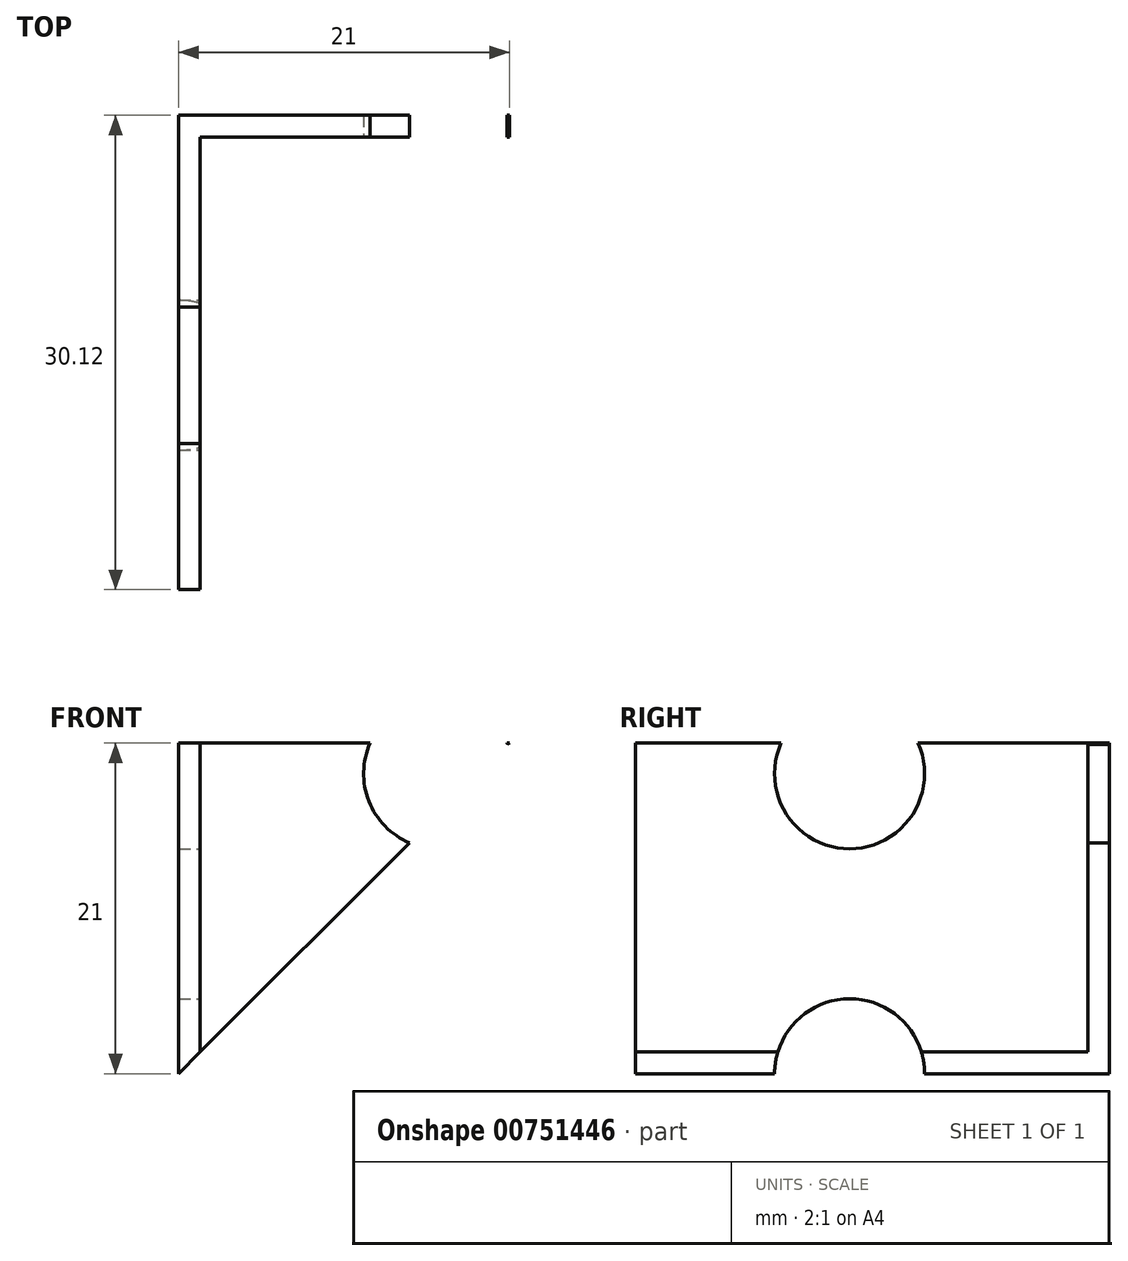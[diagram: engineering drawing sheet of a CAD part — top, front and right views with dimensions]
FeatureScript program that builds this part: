
annotation { "Feature Type Name" : "Feature", "Feature Type Description" : "" }
export const myFeature = defineFeature(function(context is Context, id is Id, definition is map)
    precondition{}
    {
        {
            assignVariable(context, id + "F0", {"name" : "height", "anyValue" : 21});
        }
        {
            var Q0;
            Q0=qCreatedBy(makeId("Top.planeOp"),FACE);
            var sketch = newSketch(context, id + "F1", { "sketchPlane" : qUnion([Q0])});
            skLineSegment(sketch, "E0", {"start": v(-1.37, -28.75) * mm, "end": v(-1.37, 1.37) * mm});
            skLineSegment(sketch, "E1", {"start": v(-1.37, 1.37) * mm, "end": v(28.75, 1.37) * mm});
            skLineSegment(sketch, "E2", {"start": v(28.75, 1.37) * mm, "end": v(28.75, 0) * mm});
            skLineSegment(sketch, "E3", {"start": v(28.75, 0) * mm, "end": v(0, 0) * mm});
            skLineSegment(sketch, "E4", {"start": v(0, 0) * mm, "end": v(0, -28.75) * mm});
            skLineSegment(sketch, "E5", {"start": v(0, -28.75) * mm, "end": v(-1.37, -28.75) * mm});
            skSolve(sketch);
        }
        {
            var Q0;
            Q0=makeQuery(id+"F1.imprint","IMPRINT",FACE,{"disambiguationData":[TD([[makeQuery(id+"F1.imprint","IMPRINT",EDGE,{"derivedFrom":sQuery(id+"F1.wireOp",EDGE,"E0")}),-1.0]])]});
            extrude(context, id + "F2", {"entities" : qUnion([Q0]), "depth" : (getVariable(context, 'height')) * mm, "offsetDistance" : 25.4 * mm});
        }
        {
            var Q0;
            Q0=makeQuery(id+"F2.opExtrude","SWEPT_FACE",FACE,{"disambiguationData":[OSD([sQuery(id+"F1.wireOp",EDGE,"E3")])]});
            var sketch = newSketch(context, id + "F3", { "sketchPlane" : qUnion([Q0])});
            skPoint(sketch, "E6", {"position": v(15.14, 19.05) * mm});
            skLineSegment(sketch, "E7", {"start": v(15.14, 0) * mm, "end": v(15.14, 533.4) * mm, "construction": true});
            skCircle(sketch, "E8", {"center": v(15.14, 19.05) * mm, "radius": 4.76 * mm});
            skCircle(sketch, "E9", {"center": v(15.14, 0) * mm, "radius": 4.76 * mm});
            skPoint(sketch, "E10", {"position": v(15.14, 38.1) * mm});
            skPoint(sketch, "E11", {"position": v(15.14, 57.15) * mm});
            skArc(sketch, "E12", {"start": v(19.9, 39.69) * mm, "mid": v(15.14, 44.45) * mm, "end": v(10.38, 39.69) * mm});
            skArc(sketch, "E13", {"start": v(10.38, 36.51) * mm, "mid": v(15.14, 31.75) * mm, "end": v(19.9, 36.51) * mm});
            skLineSegment(sketch, "E14", {"start": v(19.9, 39.69) * mm, "end": v(19.9, 36.51) * mm});
            skLineSegment(sketch, "E15", {"start": v(10.38, 39.69) * mm, "end": v(10.38, 36.51) * mm});
            skArc(sketch, "E16", {"start": v(19.9, 58.74) * mm, "mid": v(15.14, 63.5) * mm, "end": v(10.38, 58.74) * mm});
            skArc(sketch, "E17", {"start": v(10.38, 55.56) * mm, "mid": v(15.14, 50.8) * mm, "end": v(19.9, 55.56) * mm});
            skLineSegment(sketch, "E18", {"start": v(19.9, 58.74) * mm, "end": v(19.9, 55.56) * mm});
            skLineSegment(sketch, "E19", {"start": v(10.38, 58.74) * mm, "end": v(10.38, 55.56) * mm});
            skPoint(sketch, "E20.0.1.0", {"position": v(15.14, 133.35) * mm});
            skArc(sketch, "E20.0.1.1", {"start": v(19.9, 134.94) * mm, "mid": v(15.14, 139.7) * mm, "end": v(10.38, 134.94) * mm});
            skPoint(sketch, "E20.0.1.2", {"position": v(15.14, 114.3) * mm});
            skPoint(sketch, "E20.0.1.3", {"position": v(15.14, 95.25) * mm});
            skArc(sketch, "E20.0.1.4", {"start": v(10.38, 131.76) * mm, "mid": v(15.14, 127) * mm, "end": v(19.9, 131.76) * mm});
            skCircle(sketch, "E20.0.1.5", {"center": v(15.14, 95.25) * mm, "radius": 4.76 * mm});
            skCircle(sketch, "E20.0.1.6", {"center": v(15.14, 76.2) * mm, "radius": 4.76 * mm});
            skArc(sketch, "E20.0.1.7", {"start": v(19.9, 115.89) * mm, "mid": v(15.14, 120.65) * mm, "end": v(10.38, 115.89) * mm});
            skArc(sketch, "E20.0.1.8", {"start": v(10.38, 112.71) * mm, "mid": v(15.14, 107.95) * mm, "end": v(19.9, 112.71) * mm});
            skPoint(sketch, "E20.0.1.9", {"position": v(15.14, 133.35) * mm});
            skPoint(sketch, "E20.0.1.10", {"position": v(15.14, 114.3) * mm});
            skLineSegment(sketch, "E20.0.1.11", {"start": v(10.38, 134.94) * mm, "end": v(10.38, 131.76) * mm});
            skLineSegment(sketch, "E20.0.1.12", {"start": v(19.9, 134.94) * mm, "end": v(19.9, 131.76) * mm});
            skLineSegment(sketch, "E20.0.1.13", {"start": v(19.9, 115.89) * mm, "end": v(19.9, 112.71) * mm});
            skLineSegment(sketch, "E20.0.1.14", {"start": v(10.38, 115.89) * mm, "end": v(10.38, 112.71) * mm});
            skPoint(sketch, "E20.0.2.0", {"position": v(15.14, 209.55) * mm});
            skArc(sketch, "E20.0.2.1", {"start": v(19.9, 211.14) * mm, "mid": v(15.14, 215.9) * mm, "end": v(10.38, 211.14) * mm});
            skPoint(sketch, "E20.0.2.2", {"position": v(15.14, 190.5) * mm});
            skPoint(sketch, "E20.0.2.3", {"position": v(15.14, 171.45) * mm});
            skArc(sketch, "E20.0.2.4", {"start": v(10.38, 207.96) * mm, "mid": v(15.14, 203.2) * mm, "end": v(19.9, 207.96) * mm});
            skCircle(sketch, "E20.0.2.5", {"center": v(15.14, 171.45) * mm, "radius": 4.76 * mm});
            skCircle(sketch, "E20.0.2.6", {"center": v(15.14, 152.4) * mm, "radius": 4.76 * mm});
            skArc(sketch, "E20.0.2.7", {"start": v(19.9, 192.09) * mm, "mid": v(15.14, 196.85) * mm, "end": v(10.38, 192.09) * mm});
            skArc(sketch, "E20.0.2.8", {"start": v(10.38, 188.91) * mm, "mid": v(15.14, 184.15) * mm, "end": v(19.9, 188.91) * mm});
            skPoint(sketch, "E20.0.2.9", {"position": v(15.14, 209.55) * mm});
            skPoint(sketch, "E20.0.2.10", {"position": v(15.14, 190.5) * mm});
            skLineSegment(sketch, "E20.0.2.11", {"start": v(10.38, 211.14) * mm, "end": v(10.38, 207.96) * mm});
            skLineSegment(sketch, "E20.0.2.12", {"start": v(19.9, 211.14) * mm, "end": v(19.9, 207.96) * mm});
            skLineSegment(sketch, "E20.0.2.13", {"start": v(19.9, 192.09) * mm, "end": v(19.9, 188.91) * mm});
            skLineSegment(sketch, "E20.0.2.14", {"start": v(10.38, 192.09) * mm, "end": v(10.38, 188.91) * mm});
            skPoint(sketch, "E20.0.3.0", {"position": v(15.14, 285.75) * mm});
            skArc(sketch, "E20.0.3.1", {"start": v(19.9, 287.34) * mm, "mid": v(15.14, 292.1) * mm, "end": v(10.38, 287.34) * mm});
            skPoint(sketch, "E20.0.3.2", {"position": v(15.14, 266.7) * mm});
            skPoint(sketch, "E20.0.3.3", {"position": v(15.14, 247.65) * mm});
            skArc(sketch, "E20.0.3.4", {"start": v(10.38, 284.16) * mm, "mid": v(15.14, 279.4) * mm, "end": v(19.9, 284.16) * mm});
            skCircle(sketch, "E20.0.3.5", {"center": v(15.14, 247.65) * mm, "radius": 4.76 * mm});
            skCircle(sketch, "E20.0.3.6", {"center": v(15.14, 228.6) * mm, "radius": 4.76 * mm});
            skArc(sketch, "E20.0.3.7", {"start": v(19.9, 268.29) * mm, "mid": v(15.14, 273.05) * mm, "end": v(10.38, 268.29) * mm});
            skArc(sketch, "E20.0.3.8", {"start": v(10.38, 265.11) * mm, "mid": v(15.14, 260.35) * mm, "end": v(19.9, 265.11) * mm});
            skPoint(sketch, "E20.0.3.9", {"position": v(15.14, 285.75) * mm});
            skPoint(sketch, "E20.0.3.10", {"position": v(15.14, 266.7) * mm});
            skLineSegment(sketch, "E20.0.3.11", {"start": v(10.38, 287.34) * mm, "end": v(10.38, 284.16) * mm});
            skLineSegment(sketch, "E20.0.3.12", {"start": v(19.9, 287.34) * mm, "end": v(19.9, 284.16) * mm});
            skLineSegment(sketch, "E20.0.3.13", {"start": v(19.9, 268.29) * mm, "end": v(19.9, 265.11) * mm});
            skLineSegment(sketch, "E20.0.3.14", {"start": v(10.38, 268.29) * mm, "end": v(10.38, 265.11) * mm});
            skPoint(sketch, "E20.0.4.0", {"position": v(15.14, 361.95) * mm});
            skArc(sketch, "E20.0.4.1", {"start": v(19.9, 363.54) * mm, "mid": v(15.14, 368.3) * mm, "end": v(10.38, 363.54) * mm});
            skPoint(sketch, "E20.0.4.2", {"position": v(15.14, 342.9) * mm});
            skPoint(sketch, "E20.0.4.3", {"position": v(15.14, 323.85) * mm});
            skArc(sketch, "E20.0.4.4", {"start": v(10.38, 360.36) * mm, "mid": v(15.14, 355.6) * mm, "end": v(19.9, 360.36) * mm});
            skCircle(sketch, "E20.0.4.5", {"center": v(15.14, 323.85) * mm, "radius": 4.76 * mm});
            skCircle(sketch, "E20.0.4.6", {"center": v(15.14, 304.8) * mm, "radius": 4.76 * mm});
            skArc(sketch, "E20.0.4.7", {"start": v(19.9, 344.49) * mm, "mid": v(15.14, 349.25) * mm, "end": v(10.38, 344.49) * mm});
            skArc(sketch, "E20.0.4.8", {"start": v(10.38, 341.31) * mm, "mid": v(15.14, 336.55) * mm, "end": v(19.9, 341.31) * mm});
            skPoint(sketch, "E20.0.4.9", {"position": v(15.14, 361.95) * mm});
            skPoint(sketch, "E20.0.4.10", {"position": v(15.14, 342.9) * mm});
            skLineSegment(sketch, "E20.0.4.11", {"start": v(10.38, 363.54) * mm, "end": v(10.38, 360.36) * mm});
            skLineSegment(sketch, "E20.0.4.12", {"start": v(19.9, 363.54) * mm, "end": v(19.9, 360.36) * mm});
            skLineSegment(sketch, "E20.0.4.13", {"start": v(19.9, 344.49) * mm, "end": v(19.9, 341.31) * mm});
            skLineSegment(sketch, "E20.0.4.14", {"start": v(10.38, 344.49) * mm, "end": v(10.38, 341.31) * mm});
            skPoint(sketch, "E20.0.5.0", {"position": v(15.14, 438.15) * mm});
            skArc(sketch, "E20.0.5.1", {"start": v(19.9, 439.74) * mm, "mid": v(15.14, 444.5) * mm, "end": v(10.38, 439.74) * mm});
            skPoint(sketch, "E20.0.5.2", {"position": v(15.14, 419.1) * mm});
            skPoint(sketch, "E20.0.5.3", {"position": v(15.14, 400.05) * mm});
            skArc(sketch, "E20.0.5.4", {"start": v(10.38, 436.56) * mm, "mid": v(15.14, 431.8) * mm, "end": v(19.9, 436.56) * mm});
            skCircle(sketch, "E20.0.5.5", {"center": v(15.14, 400.05) * mm, "radius": 4.76 * mm});
            skCircle(sketch, "E20.0.5.6", {"center": v(15.14, 381) * mm, "radius": 4.76 * mm});
            skArc(sketch, "E20.0.5.7", {"start": v(19.9, 420.69) * mm, "mid": v(15.14, 425.45) * mm, "end": v(10.38, 420.69) * mm});
            skArc(sketch, "E20.0.5.8", {"start": v(10.38, 417.51) * mm, "mid": v(15.14, 412.75) * mm, "end": v(19.9, 417.51) * mm});
            skPoint(sketch, "E20.0.5.9", {"position": v(15.14, 438.15) * mm});
            skPoint(sketch, "E20.0.5.10", {"position": v(15.14, 419.1) * mm});
            skLineSegment(sketch, "E20.0.5.11", {"start": v(10.38, 439.74) * mm, "end": v(10.38, 436.56) * mm});
            skLineSegment(sketch, "E20.0.5.12", {"start": v(19.9, 439.74) * mm, "end": v(19.9, 436.56) * mm});
            skLineSegment(sketch, "E20.0.5.13", {"start": v(19.9, 420.69) * mm, "end": v(19.9, 417.51) * mm});
            skLineSegment(sketch, "E20.0.5.14", {"start": v(10.38, 420.69) * mm, "end": v(10.38, 417.51) * mm});
            skPoint(sketch, "E20.0.6.0", {"position": v(15.14, 514.35) * mm});
            skArc(sketch, "E20.0.6.1", {"start": v(19.9, 515.94) * mm, "mid": v(15.14, 520.7) * mm, "end": v(10.38, 515.94) * mm});
            skPoint(sketch, "E20.0.6.2", {"position": v(15.14, 495.3) * mm});
            skPoint(sketch, "E20.0.6.3", {"position": v(15.14, 476.25) * mm});
            skArc(sketch, "E20.0.6.4", {"start": v(10.38, 512.76) * mm, "mid": v(15.14, 508) * mm, "end": v(19.9, 512.76) * mm});
            skCircle(sketch, "E20.0.6.5", {"center": v(15.14, 476.25) * mm, "radius": 4.76 * mm});
            skCircle(sketch, "E20.0.6.6", {"center": v(15.14, 457.2) * mm, "radius": 4.76 * mm});
            skArc(sketch, "E20.0.6.7", {"start": v(19.9, 496.89) * mm, "mid": v(15.14, 501.65) * mm, "end": v(10.38, 496.89) * mm});
            skArc(sketch, "E20.0.6.8", {"start": v(10.38, 493.71) * mm, "mid": v(15.14, 488.95) * mm, "end": v(19.9, 493.71) * mm});
            skPoint(sketch, "E20.0.6.9", {"position": v(15.14, 514.35) * mm});
            skPoint(sketch, "E20.0.6.10", {"position": v(15.14, 495.3) * mm});
            skLineSegment(sketch, "E20.0.6.11", {"start": v(10.38, 515.94) * mm, "end": v(10.38, 512.76) * mm});
            skLineSegment(sketch, "E20.0.6.12", {"start": v(19.9, 515.94) * mm, "end": v(19.9, 512.76) * mm});
            skLineSegment(sketch, "E20.0.6.13", {"start": v(19.9, 496.89) * mm, "end": v(19.9, 493.71) * mm});
            skLineSegment(sketch, "E20.0.6.14", {"start": v(10.38, 496.89) * mm, "end": v(10.38, 493.71) * mm});
            skPoint(sketch, "E20.0.7.0", {"position": v(15.14, 590.55) * mm});
            skArc(sketch, "E20.0.7.1", {"start": v(19.9, 592.14) * mm, "mid": v(15.14, 596.9) * mm, "end": v(10.38, 592.14) * mm});
            skPoint(sketch, "E20.0.7.2", {"position": v(15.14, 571.5) * mm});
            skPoint(sketch, "E20.0.7.3", {"position": v(15.14, 552.45) * mm});
            skArc(sketch, "E20.0.7.4", {"start": v(10.38, 588.96) * mm, "mid": v(15.14, 584.2) * mm, "end": v(19.9, 588.96) * mm});
            skCircle(sketch, "E20.0.7.5", {"center": v(15.14, 552.45) * mm, "radius": 4.76 * mm});
            skCircle(sketch, "E20.0.7.6", {"center": v(15.14, 533.4) * mm, "radius": 4.76 * mm});
            skArc(sketch, "E20.0.7.7", {"start": v(19.9, 573.09) * mm, "mid": v(15.14, 577.85) * mm, "end": v(10.38, 573.09) * mm});
            skArc(sketch, "E20.0.7.8", {"start": v(10.38, 569.91) * mm, "mid": v(15.14, 565.15) * mm, "end": v(19.9, 569.91) * mm});
            skPoint(sketch, "E20.0.7.9", {"position": v(15.14, 590.55) * mm});
            skPoint(sketch, "E20.0.7.10", {"position": v(15.14, 571.5) * mm});
            skLineSegment(sketch, "E20.0.7.11", {"start": v(10.38, 592.14) * mm, "end": v(10.38, 588.96) * mm});
            skLineSegment(sketch, "E20.0.7.12", {"start": v(19.9, 592.14) * mm, "end": v(19.9, 588.96) * mm});
            skLineSegment(sketch, "E20.0.7.13", {"start": v(19.9, 573.09) * mm, "end": v(19.9, 569.91) * mm});
            skLineSegment(sketch, "E20.0.7.14", {"start": v(10.38, 573.09) * mm, "end": v(10.38, 569.91) * mm});
            skPoint(sketch, "E20.0.8.0", {"position": v(15.14, 666.75) * mm});
            skArc(sketch, "E20.0.8.1", {"start": v(19.9, 668.34) * mm, "mid": v(15.14, 673.1) * mm, "end": v(10.38, 668.34) * mm});
            skPoint(sketch, "E20.0.8.2", {"position": v(15.14, 647.7) * mm});
            skPoint(sketch, "E20.0.8.3", {"position": v(15.14, 628.65) * mm});
            skArc(sketch, "E20.0.8.4", {"start": v(10.38, 665.16) * mm, "mid": v(15.14, 660.4) * mm, "end": v(19.9, 665.16) * mm});
            skCircle(sketch, "E20.0.8.5", {"center": v(15.14, 628.65) * mm, "radius": 4.76 * mm});
            skCircle(sketch, "E20.0.8.6", {"center": v(15.14, 609.6) * mm, "radius": 4.76 * mm});
            skArc(sketch, "E20.0.8.7", {"start": v(19.9, 649.29) * mm, "mid": v(15.14, 654.05) * mm, "end": v(10.38, 649.29) * mm});
            skArc(sketch, "E20.0.8.8", {"start": v(10.38, 646.11) * mm, "mid": v(15.14, 641.35) * mm, "end": v(19.9, 646.11) * mm});
            skPoint(sketch, "E20.0.8.9", {"position": v(15.14, 666.75) * mm});
            skPoint(sketch, "E20.0.8.10", {"position": v(15.14, 647.7) * mm});
            skLineSegment(sketch, "E20.0.8.11", {"start": v(10.38, 668.34) * mm, "end": v(10.38, 665.16) * mm});
            skLineSegment(sketch, "E20.0.8.12", {"start": v(19.9, 668.34) * mm, "end": v(19.9, 665.16) * mm});
            skLineSegment(sketch, "E20.0.8.13", {"start": v(19.9, 649.29) * mm, "end": v(19.9, 646.11) * mm});
            skLineSegment(sketch, "E20.0.8.14", {"start": v(10.38, 649.29) * mm, "end": v(10.38, 646.11) * mm});
            skPoint(sketch, "E20.0.9.0", {"position": v(15.14, 742.95) * mm});
            skArc(sketch, "E20.0.9.1", {"start": v(19.9, 744.54) * mm, "mid": v(15.14, 749.3) * mm, "end": v(10.38, 744.54) * mm});
            skPoint(sketch, "E20.0.9.2", {"position": v(15.14, 723.9) * mm});
            skPoint(sketch, "E20.0.9.3", {"position": v(15.14, 704.85) * mm});
            skArc(sketch, "E20.0.9.4", {"start": v(10.38, 741.36) * mm, "mid": v(15.14, 736.6) * mm, "end": v(19.9, 741.36) * mm});
            skCircle(sketch, "E20.0.9.5", {"center": v(15.14, 704.85) * mm, "radius": 4.76 * mm});
            skCircle(sketch, "E20.0.9.6", {"center": v(15.14, 685.8) * mm, "radius": 4.76 * mm});
            skArc(sketch, "E20.0.9.7", {"start": v(19.9, 725.49) * mm, "mid": v(15.14, 730.25) * mm, "end": v(10.38, 725.49) * mm});
            skArc(sketch, "E20.0.9.8", {"start": v(10.38, 722.31) * mm, "mid": v(15.14, 717.55) * mm, "end": v(19.9, 722.31) * mm});
            skPoint(sketch, "E20.0.9.9", {"position": v(15.14, 742.95) * mm});
            skPoint(sketch, "E20.0.9.10", {"position": v(15.14, 723.9) * mm});
            skLineSegment(sketch, "E20.0.9.11", {"start": v(10.38, 744.54) * mm, "end": v(10.38, 741.36) * mm});
            skLineSegment(sketch, "E20.0.9.12", {"start": v(19.9, 744.54) * mm, "end": v(19.9, 741.36) * mm});
            skLineSegment(sketch, "E20.0.9.13", {"start": v(19.9, 725.49) * mm, "end": v(19.9, 722.31) * mm});
            skLineSegment(sketch, "E20.0.9.14", {"start": v(10.38, 725.49) * mm, "end": v(10.38, 722.31) * mm});
            skPoint(sketch, "E20.0.10.0", {"position": v(15.14, 819.15) * mm});
            skArc(sketch, "E20.0.10.1", {"start": v(19.9, 820.74) * mm, "mid": v(15.14, 825.5) * mm, "end": v(10.38, 820.74) * mm});
            skPoint(sketch, "E20.0.10.2", {"position": v(15.14, 800.1) * mm});
            skPoint(sketch, "E20.0.10.3", {"position": v(15.14, 781.05) * mm});
            skArc(sketch, "E20.0.10.4", {"start": v(10.38, 817.56) * mm, "mid": v(15.14, 812.8) * mm, "end": v(19.9, 817.56) * mm});
            skCircle(sketch, "E20.0.10.5", {"center": v(15.14, 781.05) * mm, "radius": 4.76 * mm});
            skCircle(sketch, "E20.0.10.6", {"center": v(15.14, 762) * mm, "radius": 4.76 * mm});
            skArc(sketch, "E20.0.10.7", {"start": v(19.9, 801.69) * mm, "mid": v(15.14, 806.45) * mm, "end": v(10.38, 801.69) * mm});
            skArc(sketch, "E20.0.10.8", {"start": v(10.38, 798.51) * mm, "mid": v(15.14, 793.75) * mm, "end": v(19.9, 798.51) * mm});
            skPoint(sketch, "E20.0.10.9", {"position": v(15.14, 819.15) * mm});
            skPoint(sketch, "E20.0.10.10", {"position": v(15.14, 800.1) * mm});
            skLineSegment(sketch, "E20.0.10.11", {"start": v(10.38, 820.74) * mm, "end": v(10.38, 817.56) * mm});
            skLineSegment(sketch, "E20.0.10.12", {"start": v(19.9, 820.74) * mm, "end": v(19.9, 817.56) * mm});
            skLineSegment(sketch, "E20.0.10.13", {"start": v(19.9, 801.69) * mm, "end": v(19.9, 798.51) * mm});
            skLineSegment(sketch, "E20.0.10.14", {"start": v(10.38, 801.69) * mm, "end": v(10.38, 798.51) * mm});
            skPoint(sketch, "E20.0.11.0", {"position": v(15.14, 895.35) * mm});
            skArc(sketch, "E20.0.11.1", {"start": v(19.9, 896.94) * mm, "mid": v(15.14, 901.7) * mm, "end": v(10.38, 896.94) * mm});
            skPoint(sketch, "E20.0.11.2", {"position": v(15.14, 876.3) * mm});
            skPoint(sketch, "E20.0.11.3", {"position": v(15.14, 857.25) * mm});
            skArc(sketch, "E20.0.11.4", {"start": v(10.38, 893.76) * mm, "mid": v(15.14, 889) * mm, "end": v(19.9, 893.76) * mm});
            skCircle(sketch, "E20.0.11.5", {"center": v(15.14, 857.25) * mm, "radius": 4.76 * mm});
            skCircle(sketch, "E20.0.11.6", {"center": v(15.14, 838.2) * mm, "radius": 4.76 * mm});
            skArc(sketch, "E20.0.11.7", {"start": v(19.9, 877.89) * mm, "mid": v(15.14, 882.65) * mm, "end": v(10.38, 877.89) * mm});
            skArc(sketch, "E20.0.11.8", {"start": v(10.38, 874.71) * mm, "mid": v(15.14, 869.95) * mm, "end": v(19.9, 874.71) * mm});
            skPoint(sketch, "E20.0.11.9", {"position": v(15.14, 895.35) * mm});
            skPoint(sketch, "E20.0.11.10", {"position": v(15.14, 876.3) * mm});
            skLineSegment(sketch, "E20.0.11.11", {"start": v(10.38, 896.94) * mm, "end": v(10.38, 893.76) * mm});
            skLineSegment(sketch, "E20.0.11.12", {"start": v(19.9, 896.94) * mm, "end": v(19.9, 893.76) * mm});
            skLineSegment(sketch, "E20.0.11.13", {"start": v(19.9, 877.89) * mm, "end": v(19.9, 874.71) * mm});
            skLineSegment(sketch, "E20.0.11.14", {"start": v(10.38, 877.89) * mm, "end": v(10.38, 874.71) * mm});
            skPoint(sketch, "E20.0.12.0", {"position": v(15.14, 971.55) * mm});
            skArc(sketch, "E20.0.12.1", {"start": v(19.9, 973.14) * mm, "mid": v(15.14, 977.9) * mm, "end": v(10.38, 973.14) * mm});
            skPoint(sketch, "E20.0.12.2", {"position": v(15.14, 952.5) * mm});
            skPoint(sketch, "E20.0.12.3", {"position": v(15.14, 933.45) * mm});
            skArc(sketch, "E20.0.12.4", {"start": v(10.38, 969.96) * mm, "mid": v(15.14, 965.2) * mm, "end": v(19.9, 969.96) * mm});
            skCircle(sketch, "E20.0.12.5", {"center": v(15.14, 933.45) * mm, "radius": 4.76 * mm});
            skCircle(sketch, "E20.0.12.6", {"center": v(15.14, 914.4) * mm, "radius": 4.76 * mm});
            skArc(sketch, "E20.0.12.7", {"start": v(19.9, 954.09) * mm, "mid": v(15.14, 958.85) * mm, "end": v(10.38, 954.09) * mm});
            skArc(sketch, "E20.0.12.8", {"start": v(10.38, 950.91) * mm, "mid": v(15.14, 946.15) * mm, "end": v(19.9, 950.91) * mm});
            skPoint(sketch, "E20.0.12.9", {"position": v(15.14, 971.55) * mm});
            skPoint(sketch, "E20.0.12.10", {"position": v(15.14, 952.5) * mm});
            skLineSegment(sketch, "E20.0.12.11", {"start": v(10.38, 973.14) * mm, "end": v(10.38, 969.96) * mm});
            skLineSegment(sketch, "E20.0.12.12", {"start": v(19.9, 973.14) * mm, "end": v(19.9, 969.96) * mm});
            skLineSegment(sketch, "E20.0.12.13", {"start": v(19.9, 954.09) * mm, "end": v(19.9, 950.91) * mm});
            skLineSegment(sketch, "E20.0.12.14", {"start": v(10.38, 954.09) * mm, "end": v(10.38, 950.91) * mm});
            skPoint(sketch, "E20.0.13.0", {"position": v(15.14, 1047.75) * mm});
            skArc(sketch, "E20.0.13.1", {"start": v(19.9, 1049.34) * mm, "mid": v(15.14, 1054.1) * mm, "end": v(10.38, 1049.34) * mm});
            skPoint(sketch, "E20.0.13.2", {"position": v(15.14, 1028.7) * mm});
            skPoint(sketch, "E20.0.13.3", {"position": v(15.14, 1009.65) * mm});
            skArc(sketch, "E20.0.13.4", {"start": v(10.38, 1046.16) * mm, "mid": v(15.14, 1041.4) * mm, "end": v(19.9, 1046.16) * mm});
            skCircle(sketch, "E20.0.13.5", {"center": v(15.14, 1009.65) * mm, "radius": 4.76 * mm});
            skCircle(sketch, "E20.0.13.6", {"center": v(15.14, 990.6) * mm, "radius": 4.76 * mm});
            skArc(sketch, "E20.0.13.7", {"start": v(19.9, 1030.29) * mm, "mid": v(15.14, 1035.05) * mm, "end": v(10.38, 1030.29) * mm});
            skArc(sketch, "E20.0.13.8", {"start": v(10.38, 1027.11) * mm, "mid": v(15.14, 1022.35) * mm, "end": v(19.9, 1027.11) * mm});
            skPoint(sketch, "E20.0.13.9", {"position": v(15.14, 1047.75) * mm});
            skPoint(sketch, "E20.0.13.10", {"position": v(15.14, 1028.7) * mm});
            skLineSegment(sketch, "E20.0.13.11", {"start": v(10.38, 1049.34) * mm, "end": v(10.38, 1046.16) * mm});
            skLineSegment(sketch, "E20.0.13.12", {"start": v(19.9, 1049.34) * mm, "end": v(19.9, 1046.16) * mm});
            skLineSegment(sketch, "E20.0.13.13", {"start": v(19.9, 1030.29) * mm, "end": v(19.9, 1027.11) * mm});
            skLineSegment(sketch, "E20.0.13.14", {"start": v(10.38, 1030.29) * mm, "end": v(10.38, 1027.11) * mm});
            skPoint(sketch, "E20.0.14.0", {"position": v(15.14, 1123.95) * mm});
            skArc(sketch, "E20.0.14.1", {"start": v(19.9, 1125.54) * mm, "mid": v(15.14, 1130.3) * mm, "end": v(10.38, 1125.54) * mm});
            skPoint(sketch, "E20.0.14.2", {"position": v(15.14, 1104.9) * mm});
            skPoint(sketch, "E20.0.14.3", {"position": v(15.14, 1085.85) * mm});
            skArc(sketch, "E20.0.14.4", {"start": v(10.38, 1122.36) * mm, "mid": v(15.14, 1117.6) * mm, "end": v(19.9, 1122.36) * mm});
            skCircle(sketch, "E20.0.14.5", {"center": v(15.14, 1085.85) * mm, "radius": 4.76 * mm});
            skCircle(sketch, "E20.0.14.6", {"center": v(15.14, 1066.8) * mm, "radius": 4.76 * mm});
            skArc(sketch, "E20.0.14.7", {"start": v(19.9, 1106.49) * mm, "mid": v(15.14, 1111.25) * mm, "end": v(10.38, 1106.49) * mm});
            skArc(sketch, "E20.0.14.8", {"start": v(10.38, 1103.31) * mm, "mid": v(15.14, 1098.55) * mm, "end": v(19.9, 1103.31) * mm});
            skPoint(sketch, "E20.0.14.9", {"position": v(15.14, 1123.95) * mm});
            skPoint(sketch, "E20.0.14.10", {"position": v(15.14, 1104.9) * mm});
            skLineSegment(sketch, "E20.0.14.11", {"start": v(10.38, 1125.54) * mm, "end": v(10.38, 1122.36) * mm});
            skLineSegment(sketch, "E20.0.14.12", {"start": v(19.9, 1125.54) * mm, "end": v(19.9, 1122.36) * mm});
            skLineSegment(sketch, "E20.0.14.13", {"start": v(19.9, 1106.49) * mm, "end": v(19.9, 1103.31) * mm});
            skLineSegment(sketch, "E20.0.14.14", {"start": v(10.38, 1106.49) * mm, "end": v(10.38, 1103.31) * mm});
            skPoint(sketch, "E20.0.15.0", {"position": v(15.14, 1200.15) * mm});
            skArc(sketch, "E20.0.15.1", {"start": v(19.9, 1201.74) * mm, "mid": v(15.14, 1206.5) * mm, "end": v(10.38, 1201.74) * mm});
            skPoint(sketch, "E20.0.15.2", {"position": v(15.14, 1181.1) * mm});
            skPoint(sketch, "E20.0.15.3", {"position": v(15.14, 1162.05) * mm});
            skArc(sketch, "E20.0.15.4", {"start": v(10.38, 1198.56) * mm, "mid": v(15.14, 1193.8) * mm, "end": v(19.9, 1198.56) * mm});
            skCircle(sketch, "E20.0.15.5", {"center": v(15.14, 1162.05) * mm, "radius": 4.76 * mm});
            skCircle(sketch, "E20.0.15.6", {"center": v(15.14, 1143) * mm, "radius": 4.76 * mm});
            skArc(sketch, "E20.0.15.7", {"start": v(19.9, 1182.69) * mm, "mid": v(15.14, 1187.45) * mm, "end": v(10.38, 1182.69) * mm});
            skArc(sketch, "E20.0.15.8", {"start": v(10.38, 1179.51) * mm, "mid": v(15.14, 1174.75) * mm, "end": v(19.9, 1179.51) * mm});
            skPoint(sketch, "E20.0.15.9", {"position": v(15.14, 1200.15) * mm});
            skPoint(sketch, "E20.0.15.10", {"position": v(15.14, 1181.1) * mm});
            skLineSegment(sketch, "E20.0.15.11", {"start": v(10.38, 1201.74) * mm, "end": v(10.38, 1198.56) * mm});
            skLineSegment(sketch, "E20.0.15.12", {"start": v(19.9, 1201.74) * mm, "end": v(19.9, 1198.56) * mm});
            skLineSegment(sketch, "E20.0.15.13", {"start": v(19.9, 1182.69) * mm, "end": v(19.9, 1179.51) * mm});
            skLineSegment(sketch, "E20.0.15.14", {"start": v(10.38, 1182.69) * mm, "end": v(10.38, 1179.51) * mm});
            skPoint(sketch, "E20.0.16.0", {"position": v(15.14, 1276.35) * mm});
            skArc(sketch, "E20.0.16.1", {"start": v(19.9, 1277.94) * mm, "mid": v(15.14, 1282.7) * mm, "end": v(10.38, 1277.94) * mm});
            skPoint(sketch, "E20.0.16.2", {"position": v(15.14, 1257.3) * mm});
            skPoint(sketch, "E20.0.16.3", {"position": v(15.14, 1238.25) * mm});
            skArc(sketch, "E20.0.16.4", {"start": v(10.38, 1274.76) * mm, "mid": v(15.14, 1270) * mm, "end": v(19.9, 1274.76) * mm});
            skCircle(sketch, "E20.0.16.5", {"center": v(15.14, 1238.25) * mm, "radius": 4.76 * mm});
            skCircle(sketch, "E20.0.16.6", {"center": v(15.14, 1219.2) * mm, "radius": 4.76 * mm});
            skArc(sketch, "E20.0.16.7", {"start": v(19.9, 1258.89) * mm, "mid": v(15.14, 1263.65) * mm, "end": v(10.38, 1258.89) * mm});
            skArc(sketch, "E20.0.16.8", {"start": v(10.38, 1255.71) * mm, "mid": v(15.14, 1250.95) * mm, "end": v(19.9, 1255.71) * mm});
            skPoint(sketch, "E20.0.16.9", {"position": v(15.14, 1276.35) * mm});
            skPoint(sketch, "E20.0.16.10", {"position": v(15.14, 1257.3) * mm});
            skLineSegment(sketch, "E20.0.16.11", {"start": v(10.38, 1277.94) * mm, "end": v(10.38, 1274.76) * mm});
            skLineSegment(sketch, "E20.0.16.12", {"start": v(19.9, 1277.94) * mm, "end": v(19.9, 1274.76) * mm});
            skLineSegment(sketch, "E20.0.16.13", {"start": v(19.9, 1258.89) * mm, "end": v(19.9, 1255.71) * mm});
            skLineSegment(sketch, "E20.0.16.14", {"start": v(10.38, 1258.89) * mm, "end": v(10.38, 1255.71) * mm});
            skPoint(sketch, "E20.0.17.0", {"position": v(15.14, 1352.55) * mm});
            skArc(sketch, "E20.0.17.1", {"start": v(19.9, 1354.14) * mm, "mid": v(15.14, 1358.9) * mm, "end": v(10.38, 1354.14) * mm});
            skPoint(sketch, "E20.0.17.2", {"position": v(15.14, 1333.5) * mm});
            skPoint(sketch, "E20.0.17.3", {"position": v(15.14, 1314.45) * mm});
            skArc(sketch, "E20.0.17.4", {"start": v(10.38, 1350.96) * mm, "mid": v(15.14, 1346.2) * mm, "end": v(19.9, 1350.96) * mm});
            skCircle(sketch, "E20.0.17.5", {"center": v(15.14, 1314.45) * mm, "radius": 4.76 * mm});
            skCircle(sketch, "E20.0.17.6", {"center": v(15.14, 1295.4) * mm, "radius": 4.76 * mm});
            skArc(sketch, "E20.0.17.7", {"start": v(19.9, 1335.09) * mm, "mid": v(15.14, 1339.85) * mm, "end": v(10.38, 1335.09) * mm});
            skArc(sketch, "E20.0.17.8", {"start": v(10.38, 1331.91) * mm, "mid": v(15.14, 1327.15) * mm, "end": v(19.9, 1331.91) * mm});
            skPoint(sketch, "E20.0.17.9", {"position": v(15.14, 1352.55) * mm});
            skPoint(sketch, "E20.0.17.10", {"position": v(15.14, 1333.5) * mm});
            skLineSegment(sketch, "E20.0.17.11", {"start": v(10.38, 1354.14) * mm, "end": v(10.38, 1350.96) * mm});
            skLineSegment(sketch, "E20.0.17.12", {"start": v(19.9, 1354.14) * mm, "end": v(19.9, 1350.96) * mm});
            skLineSegment(sketch, "E20.0.17.13", {"start": v(19.9, 1335.09) * mm, "end": v(19.9, 1331.91) * mm});
            skLineSegment(sketch, "E20.0.17.14", {"start": v(10.38, 1335.09) * mm, "end": v(10.38, 1331.91) * mm});
            skPoint(sketch, "E20.0.18.0", {"position": v(15.14, 1428.75) * mm});
            skArc(sketch, "E20.0.18.1", {"start": v(19.9, 1430.34) * mm, "mid": v(15.14, 1435.1) * mm, "end": v(10.38, 1430.34) * mm});
            skPoint(sketch, "E20.0.18.2", {"position": v(15.14, 1409.7) * mm});
            skPoint(sketch, "E20.0.18.3", {"position": v(15.14, 1390.65) * mm});
            skArc(sketch, "E20.0.18.4", {"start": v(10.38, 1427.16) * mm, "mid": v(15.14, 1422.4) * mm, "end": v(19.9, 1427.16) * mm});
            skCircle(sketch, "E20.0.18.5", {"center": v(15.14, 1390.65) * mm, "radius": 4.76 * mm});
            skCircle(sketch, "E20.0.18.6", {"center": v(15.14, 1371.6) * mm, "radius": 4.76 * mm});
            skArc(sketch, "E20.0.18.7", {"start": v(19.9, 1411.29) * mm, "mid": v(15.14, 1416.05) * mm, "end": v(10.38, 1411.29) * mm});
            skArc(sketch, "E20.0.18.8", {"start": v(10.38, 1408.11) * mm, "mid": v(15.14, 1403.35) * mm, "end": v(19.9, 1408.11) * mm});
            skPoint(sketch, "E20.0.18.9", {"position": v(15.14, 1428.75) * mm});
            skPoint(sketch, "E20.0.18.10", {"position": v(15.14, 1409.7) * mm});
            skLineSegment(sketch, "E20.0.18.11", {"start": v(10.38, 1430.34) * mm, "end": v(10.38, 1427.16) * mm});
            skLineSegment(sketch, "E20.0.18.12", {"start": v(19.9, 1430.34) * mm, "end": v(19.9, 1427.16) * mm});
            skLineSegment(sketch, "E20.0.18.13", {"start": v(19.9, 1411.29) * mm, "end": v(19.9, 1408.11) * mm});
            skLineSegment(sketch, "E20.0.18.14", {"start": v(10.38, 1411.29) * mm, "end": v(10.38, 1408.11) * mm});
            skPoint(sketch, "E20.0.19.0", {"position": v(15.14, 1504.95) * mm});
            skArc(sketch, "E20.0.19.1", {"start": v(19.9, 1506.54) * mm, "mid": v(15.14, 1511.3) * mm, "end": v(10.38, 1506.54) * mm});
            skPoint(sketch, "E20.0.19.2", {"position": v(15.14, 1485.9) * mm});
            skPoint(sketch, "E20.0.19.3", {"position": v(15.14, 1466.85) * mm});
            skArc(sketch, "E20.0.19.4", {"start": v(10.38, 1503.36) * mm, "mid": v(15.14, 1498.6) * mm, "end": v(19.9, 1503.36) * mm});
            skCircle(sketch, "E20.0.19.5", {"center": v(15.14, 1466.85) * mm, "radius": 4.76 * mm});
            skCircle(sketch, "E20.0.19.6", {"center": v(15.14, 1447.8) * mm, "radius": 4.76 * mm});
            skArc(sketch, "E20.0.19.7", {"start": v(19.9, 1487.49) * mm, "mid": v(15.14, 1492.25) * mm, "end": v(10.38, 1487.49) * mm});
            skArc(sketch, "E20.0.19.8", {"start": v(10.38, 1484.31) * mm, "mid": v(15.14, 1479.55) * mm, "end": v(19.9, 1484.31) * mm});
            skPoint(sketch, "E20.0.19.9", {"position": v(15.14, 1504.95) * mm});
            skPoint(sketch, "E20.0.19.10", {"position": v(15.14, 1485.9) * mm});
            skLineSegment(sketch, "E20.0.19.11", {"start": v(10.38, 1506.54) * mm, "end": v(10.38, 1503.36) * mm});
            skLineSegment(sketch, "E20.0.19.12", {"start": v(19.9, 1506.54) * mm, "end": v(19.9, 1503.36) * mm});
            skLineSegment(sketch, "E20.0.19.13", {"start": v(19.9, 1487.49) * mm, "end": v(19.9, 1484.31) * mm});
            skLineSegment(sketch, "E20.0.19.14", {"start": v(10.38, 1487.49) * mm, "end": v(10.38, 1484.31) * mm});
            skPoint(sketch, "E20.0.20.0", {"position": v(15.14, 1581.15) * mm});
            skArc(sketch, "E20.0.20.1", {"start": v(19.9, 1582.74) * mm, "mid": v(15.14, 1587.5) * mm, "end": v(10.38, 1582.74) * mm});
            skPoint(sketch, "E20.0.20.2", {"position": v(15.14, 1562.1) * mm});
            skPoint(sketch, "E20.0.20.3", {"position": v(15.14, 1543.05) * mm});
            skArc(sketch, "E20.0.20.4", {"start": v(10.38, 1579.56) * mm, "mid": v(15.14, 1574.8) * mm, "end": v(19.9, 1579.56) * mm});
            skCircle(sketch, "E20.0.20.5", {"center": v(15.14, 1543.05) * mm, "radius": 4.76 * mm});
            skCircle(sketch, "E20.0.20.6", {"center": v(15.14, 1524) * mm, "radius": 4.76 * mm});
            skArc(sketch, "E20.0.20.7", {"start": v(19.9, 1563.69) * mm, "mid": v(15.14, 1568.45) * mm, "end": v(10.38, 1563.69) * mm});
            skArc(sketch, "E20.0.20.8", {"start": v(10.38, 1560.51) * mm, "mid": v(15.14, 1555.75) * mm, "end": v(19.9, 1560.51) * mm});
            skPoint(sketch, "E20.0.20.9", {"position": v(15.14, 1581.15) * mm});
            skPoint(sketch, "E20.0.20.10", {"position": v(15.14, 1562.1) * mm});
            skLineSegment(sketch, "E20.0.20.11", {"start": v(10.38, 1582.74) * mm, "end": v(10.38, 1579.56) * mm});
            skLineSegment(sketch, "E20.0.20.12", {"start": v(19.9, 1582.74) * mm, "end": v(19.9, 1579.56) * mm});
            skLineSegment(sketch, "E20.0.20.13", {"start": v(19.9, 1563.69) * mm, "end": v(19.9, 1560.51) * mm});
            skLineSegment(sketch, "E20.0.20.14", {"start": v(10.38, 1563.69) * mm, "end": v(10.38, 1560.51) * mm});
            skPoint(sketch, "E20.0.21.0", {"position": v(15.14, 1657.35) * mm});
            skArc(sketch, "E20.0.21.1", {"start": v(19.9, 1658.94) * mm, "mid": v(15.14, 1663.7) * mm, "end": v(10.38, 1658.94) * mm});
            skPoint(sketch, "E20.0.21.2", {"position": v(15.14, 1638.3) * mm});
            skPoint(sketch, "E20.0.21.3", {"position": v(15.14, 1619.25) * mm});
            skArc(sketch, "E20.0.21.4", {"start": v(10.38, 1655.76) * mm, "mid": v(15.14, 1651) * mm, "end": v(19.9, 1655.76) * mm});
            skCircle(sketch, "E20.0.21.5", {"center": v(15.14, 1619.25) * mm, "radius": 4.76 * mm});
            skCircle(sketch, "E20.0.21.6", {"center": v(15.14, 1600.2) * mm, "radius": 4.76 * mm});
            skArc(sketch, "E20.0.21.7", {"start": v(19.9, 1639.89) * mm, "mid": v(15.14, 1644.65) * mm, "end": v(10.38, 1639.89) * mm});
            skArc(sketch, "E20.0.21.8", {"start": v(10.38, 1636.71) * mm, "mid": v(15.14, 1631.95) * mm, "end": v(19.9, 1636.71) * mm});
            skPoint(sketch, "E20.0.21.9", {"position": v(15.14, 1657.35) * mm});
            skPoint(sketch, "E20.0.21.10", {"position": v(15.14, 1638.3) * mm});
            skLineSegment(sketch, "E20.0.21.11", {"start": v(10.38, 1658.94) * mm, "end": v(10.38, 1655.76) * mm});
            skLineSegment(sketch, "E20.0.21.12", {"start": v(19.9, 1658.94) * mm, "end": v(19.9, 1655.76) * mm});
            skLineSegment(sketch, "E20.0.21.13", {"start": v(19.9, 1639.89) * mm, "end": v(19.9, 1636.71) * mm});
            skLineSegment(sketch, "E20.0.21.14", {"start": v(10.38, 1639.89) * mm, "end": v(10.38, 1636.71) * mm});
            skPoint(sketch, "E20.0.22.0", {"position": v(15.14, 1733.55) * mm});
            skArc(sketch, "E20.0.22.1", {"start": v(19.9, 1735.14) * mm, "mid": v(15.14, 1739.9) * mm, "end": v(10.38, 1735.14) * mm});
            skPoint(sketch, "E20.0.22.2", {"position": v(15.14, 1714.5) * mm});
            skPoint(sketch, "E20.0.22.3", {"position": v(15.14, 1695.45) * mm});
            skArc(sketch, "E20.0.22.4", {"start": v(10.38, 1731.96) * mm, "mid": v(15.14, 1727.2) * mm, "end": v(19.9, 1731.96) * mm});
            skCircle(sketch, "E20.0.22.5", {"center": v(15.14, 1695.45) * mm, "radius": 4.76 * mm});
            skCircle(sketch, "E20.0.22.6", {"center": v(15.14, 1676.4) * mm, "radius": 4.76 * mm});
            skArc(sketch, "E20.0.22.7", {"start": v(19.9, 1716.09) * mm, "mid": v(15.14, 1720.85) * mm, "end": v(10.38, 1716.09) * mm});
            skArc(sketch, "E20.0.22.8", {"start": v(10.38, 1712.91) * mm, "mid": v(15.14, 1708.15) * mm, "end": v(19.9, 1712.91) * mm});
            skPoint(sketch, "E20.0.22.9", {"position": v(15.14, 1733.55) * mm});
            skPoint(sketch, "E20.0.22.10", {"position": v(15.14, 1714.5) * mm});
            skLineSegment(sketch, "E20.0.22.11", {"start": v(10.38, 1735.14) * mm, "end": v(10.38, 1731.96) * mm});
            skLineSegment(sketch, "E20.0.22.12", {"start": v(19.9, 1735.14) * mm, "end": v(19.9, 1731.96) * mm});
            skLineSegment(sketch, "E20.0.22.13", {"start": v(19.9, 1716.09) * mm, "end": v(19.9, 1712.91) * mm});
            skLineSegment(sketch, "E20.0.22.14", {"start": v(10.38, 1716.09) * mm, "end": v(10.38, 1712.91) * mm});
            skPoint(sketch, "E20.0.23.0", {"position": v(15.14, 1809.75) * mm});
            skArc(sketch, "E20.0.23.1", {"start": v(19.9, 1811.34) * mm, "mid": v(15.14, 1816.1) * mm, "end": v(10.38, 1811.34) * mm});
            skPoint(sketch, "E20.0.23.2", {"position": v(15.14, 1790.7) * mm});
            skPoint(sketch, "E20.0.23.3", {"position": v(15.14, 1771.65) * mm});
            skArc(sketch, "E20.0.23.4", {"start": v(10.38, 1808.16) * mm, "mid": v(15.14, 1803.4) * mm, "end": v(19.9, 1808.16) * mm});
            skCircle(sketch, "E20.0.23.5", {"center": v(15.14, 1771.65) * mm, "radius": 4.76 * mm});
            skCircle(sketch, "E20.0.23.6", {"center": v(15.14, 1752.6) * mm, "radius": 4.76 * mm});
            skArc(sketch, "E20.0.23.7", {"start": v(19.9, 1792.29) * mm, "mid": v(15.14, 1797.05) * mm, "end": v(10.38, 1792.29) * mm});
            skArc(sketch, "E20.0.23.8", {"start": v(10.38, 1789.11) * mm, "mid": v(15.14, 1784.35) * mm, "end": v(19.9, 1789.11) * mm});
            skPoint(sketch, "E20.0.23.9", {"position": v(15.14, 1809.75) * mm});
            skPoint(sketch, "E20.0.23.10", {"position": v(15.14, 1790.7) * mm});
            skLineSegment(sketch, "E20.0.23.11", {"start": v(10.38, 1811.34) * mm, "end": v(10.38, 1808.16) * mm});
            skLineSegment(sketch, "E20.0.23.12", {"start": v(19.9, 1811.34) * mm, "end": v(19.9, 1808.16) * mm});
            skLineSegment(sketch, "E20.0.23.13", {"start": v(19.9, 1792.29) * mm, "end": v(19.9, 1789.11) * mm});
            skLineSegment(sketch, "E20.0.23.14", {"start": v(10.38, 1792.29) * mm, "end": v(10.38, 1789.11) * mm});
            skLineSegment(sketch, "E20.direction1", {"start": v(15.14, 0) * mm, "end": v(40.54, 0) * mm, "construction": true});
            skLineSegment(sketch, "E20.direction2", {"start": v(15.14, 0) * mm, "end": v(15.14, 76.2) * mm, "construction": true});
            skSolve(sketch);
        }
        {
            var Q0;
            Q0=makeQuery(id+"F2.opExtrude","SWEPT_FACE",FACE,{"disambiguationData":[OSD([sQuery(id+"F1.wireOp",EDGE,"E4")])]});
            var sketch = newSketch(context, id + "F4", { "sketchPlane" : qUnion([Q0])});
            skPoint(sketch, "E21", {"position": v(-15.14, 19.05) * mm});
            skLineSegment(sketch, "E22", {"start": v(-15.14, 0) * mm, "end": v(-15.14, 533.4) * mm, "construction": true});
            skCircle(sketch, "E23", {"center": v(-15.14, 19.05) * mm, "radius": 4.76 * mm});
            skCircle(sketch, "E24", {"center": v(-15.14, 0) * mm, "radius": 4.76 * mm});
            skPoint(sketch, "E25", {"position": v(-15.14, 38.1) * mm});
            skPoint(sketch, "E26", {"position": v(-15.14, 57.15) * mm});
            skArc(sketch, "E27", {"start": v(-10.38, 39.69) * mm, "mid": v(-15.14, 44.45) * mm, "end": v(-19.9, 39.69) * mm});
            skArc(sketch, "E28", {"start": v(-19.9, 36.51) * mm, "mid": v(-15.14, 31.75) * mm, "end": v(-10.38, 36.51) * mm});
            skLineSegment(sketch, "E29", {"start": v(-10.38, 39.69) * mm, "end": v(-10.38, 36.51) * mm});
            skLineSegment(sketch, "E30", {"start": v(-19.9, 39.69) * mm, "end": v(-19.9, 36.51) * mm});
            skArc(sketch, "E31", {"start": v(-10.38, 58.74) * mm, "mid": v(-15.14, 63.5) * mm, "end": v(-19.9, 58.74) * mm});
            skArc(sketch, "E32", {"start": v(-19.9, 55.56) * mm, "mid": v(-15.14, 50.8) * mm, "end": v(-10.38, 55.56) * mm});
            skLineSegment(sketch, "E33", {"start": v(-10.38, 58.74) * mm, "end": v(-10.38, 55.56) * mm});
            skLineSegment(sketch, "E34", {"start": v(-19.9, 58.74) * mm, "end": v(-19.9, 55.56) * mm});
            skPoint(sketch, "E35.0.1.0", {"position": v(-15.14, 133.35) * mm});
            skArc(sketch, "E35.0.1.1", {"start": v(-10.38, 134.94) * mm, "mid": v(-15.14, 139.7) * mm, "end": v(-19.9, 134.94) * mm});
            skPoint(sketch, "E35.0.1.2", {"position": v(-15.14, 114.3) * mm});
            skPoint(sketch, "E35.0.1.3", {"position": v(-15.14, 95.25) * mm});
            skArc(sketch, "E35.0.1.4", {"start": v(-19.9, 131.76) * mm, "mid": v(-15.14, 127) * mm, "end": v(-10.38, 131.76) * mm});
            skCircle(sketch, "E35.0.1.5", {"center": v(-15.14, 95.25) * mm, "radius": 4.76 * mm});
            skCircle(sketch, "E35.0.1.6", {"center": v(-15.14, 76.2) * mm, "radius": 4.76 * mm});
            skArc(sketch, "E35.0.1.7", {"start": v(-10.38, 115.89) * mm, "mid": v(-15.14, 120.65) * mm, "end": v(-19.9, 115.89) * mm});
            skArc(sketch, "E35.0.1.8", {"start": v(-19.9, 112.71) * mm, "mid": v(-15.14, 107.95) * mm, "end": v(-10.38, 112.71) * mm});
            skPoint(sketch, "E35.0.1.9", {"position": v(-15.14, 133.35) * mm});
            skPoint(sketch, "E35.0.1.10", {"position": v(-15.14, 114.3) * mm});
            skLineSegment(sketch, "E35.0.1.11", {"start": v(-19.9, 134.94) * mm, "end": v(-19.9, 131.76) * mm});
            skLineSegment(sketch, "E35.0.1.12", {"start": v(-10.38, 134.94) * mm, "end": v(-10.38, 131.76) * mm});
            skLineSegment(sketch, "E35.0.1.13", {"start": v(-10.38, 115.89) * mm, "end": v(-10.38, 112.71) * mm});
            skLineSegment(sketch, "E35.0.1.14", {"start": v(-19.9, 115.89) * mm, "end": v(-19.9, 112.71) * mm});
            skPoint(sketch, "E35.0.2.0", {"position": v(-15.14, 209.55) * mm});
            skArc(sketch, "E35.0.2.1", {"start": v(-10.38, 211.14) * mm, "mid": v(-15.14, 215.9) * mm, "end": v(-19.9, 211.14) * mm});
            skPoint(sketch, "E35.0.2.2", {"position": v(-15.14, 190.5) * mm});
            skPoint(sketch, "E35.0.2.3", {"position": v(-15.14, 171.45) * mm});
            skArc(sketch, "E35.0.2.4", {"start": v(-19.9, 207.96) * mm, "mid": v(-15.14, 203.2) * mm, "end": v(-10.38, 207.96) * mm});
            skCircle(sketch, "E35.0.2.5", {"center": v(-15.14, 171.45) * mm, "radius": 4.76 * mm});
            skCircle(sketch, "E35.0.2.6", {"center": v(-15.14, 152.4) * mm, "radius": 4.76 * mm});
            skArc(sketch, "E35.0.2.7", {"start": v(-10.38, 192.09) * mm, "mid": v(-15.14, 196.85) * mm, "end": v(-19.9, 192.09) * mm});
            skArc(sketch, "E35.0.2.8", {"start": v(-19.9, 188.91) * mm, "mid": v(-15.14, 184.15) * mm, "end": v(-10.38, 188.91) * mm});
            skPoint(sketch, "E35.0.2.9", {"position": v(-15.14, 209.55) * mm});
            skPoint(sketch, "E35.0.2.10", {"position": v(-15.14, 190.5) * mm});
            skLineSegment(sketch, "E35.0.2.11", {"start": v(-19.9, 211.14) * mm, "end": v(-19.9, 207.96) * mm});
            skLineSegment(sketch, "E35.0.2.12", {"start": v(-10.38, 211.14) * mm, "end": v(-10.38, 207.96) * mm});
            skLineSegment(sketch, "E35.0.2.13", {"start": v(-10.38, 192.09) * mm, "end": v(-10.38, 188.91) * mm});
            skLineSegment(sketch, "E35.0.2.14", {"start": v(-19.9, 192.09) * mm, "end": v(-19.9, 188.91) * mm});
            skPoint(sketch, "E35.0.3.0", {"position": v(-15.14, 285.75) * mm});
            skArc(sketch, "E35.0.3.1", {"start": v(-10.38, 287.34) * mm, "mid": v(-15.14, 292.1) * mm, "end": v(-19.9, 287.34) * mm});
            skPoint(sketch, "E35.0.3.2", {"position": v(-15.14, 266.7) * mm});
            skPoint(sketch, "E35.0.3.3", {"position": v(-15.14, 247.65) * mm});
            skArc(sketch, "E35.0.3.4", {"start": v(-19.9, 284.16) * mm, "mid": v(-15.14, 279.4) * mm, "end": v(-10.38, 284.16) * mm});
            skCircle(sketch, "E35.0.3.5", {"center": v(-15.14, 247.65) * mm, "radius": 4.76 * mm});
            skCircle(sketch, "E35.0.3.6", {"center": v(-15.14, 228.6) * mm, "radius": 4.76 * mm});
            skArc(sketch, "E35.0.3.7", {"start": v(-10.38, 268.29) * mm, "mid": v(-15.14, 273.05) * mm, "end": v(-19.9, 268.29) * mm});
            skArc(sketch, "E35.0.3.8", {"start": v(-19.9, 265.11) * mm, "mid": v(-15.14, 260.35) * mm, "end": v(-10.38, 265.11) * mm});
            skPoint(sketch, "E35.0.3.9", {"position": v(-15.14, 285.75) * mm});
            skPoint(sketch, "E35.0.3.10", {"position": v(-15.14, 266.7) * mm});
            skLineSegment(sketch, "E35.0.3.11", {"start": v(-19.9, 287.34) * mm, "end": v(-19.9, 284.16) * mm});
            skLineSegment(sketch, "E35.0.3.12", {"start": v(-10.38, 287.34) * mm, "end": v(-10.38, 284.16) * mm});
            skLineSegment(sketch, "E35.0.3.13", {"start": v(-10.38, 268.29) * mm, "end": v(-10.38, 265.11) * mm});
            skLineSegment(sketch, "E35.0.3.14", {"start": v(-19.9, 268.29) * mm, "end": v(-19.9, 265.11) * mm});
            skPoint(sketch, "E35.0.4.0", {"position": v(-15.14, 361.95) * mm});
            skArc(sketch, "E35.0.4.1", {"start": v(-10.38, 363.54) * mm, "mid": v(-15.14, 368.3) * mm, "end": v(-19.9, 363.54) * mm});
            skPoint(sketch, "E35.0.4.2", {"position": v(-15.14, 342.9) * mm});
            skPoint(sketch, "E35.0.4.3", {"position": v(-15.14, 323.85) * mm});
            skArc(sketch, "E35.0.4.4", {"start": v(-19.9, 360.36) * mm, "mid": v(-15.14, 355.6) * mm, "end": v(-10.38, 360.36) * mm});
            skCircle(sketch, "E35.0.4.5", {"center": v(-15.14, 323.85) * mm, "radius": 4.76 * mm});
            skCircle(sketch, "E35.0.4.6", {"center": v(-15.14, 304.8) * mm, "radius": 4.76 * mm});
            skArc(sketch, "E35.0.4.7", {"start": v(-10.38, 344.49) * mm, "mid": v(-15.14, 349.25) * mm, "end": v(-19.9, 344.49) * mm});
            skArc(sketch, "E35.0.4.8", {"start": v(-19.9, 341.31) * mm, "mid": v(-15.14, 336.55) * mm, "end": v(-10.38, 341.31) * mm});
            skPoint(sketch, "E35.0.4.9", {"position": v(-15.14, 361.95) * mm});
            skPoint(sketch, "E35.0.4.10", {"position": v(-15.14, 342.9) * mm});
            skLineSegment(sketch, "E35.0.4.11", {"start": v(-19.9, 363.54) * mm, "end": v(-19.9, 360.36) * mm});
            skLineSegment(sketch, "E35.0.4.12", {"start": v(-10.38, 363.54) * mm, "end": v(-10.38, 360.36) * mm});
            skLineSegment(sketch, "E35.0.4.13", {"start": v(-10.38, 344.49) * mm, "end": v(-10.38, 341.31) * mm});
            skLineSegment(sketch, "E35.0.4.14", {"start": v(-19.9, 344.49) * mm, "end": v(-19.9, 341.31) * mm});
            skPoint(sketch, "E35.0.5.0", {"position": v(-15.14, 438.15) * mm});
            skArc(sketch, "E35.0.5.1", {"start": v(-10.38, 439.74) * mm, "mid": v(-15.14, 444.5) * mm, "end": v(-19.9, 439.74) * mm});
            skPoint(sketch, "E35.0.5.2", {"position": v(-15.14, 419.1) * mm});
            skPoint(sketch, "E35.0.5.3", {"position": v(-15.14, 400.05) * mm});
            skArc(sketch, "E35.0.5.4", {"start": v(-19.9, 436.56) * mm, "mid": v(-15.14, 431.8) * mm, "end": v(-10.38, 436.56) * mm});
            skCircle(sketch, "E35.0.5.5", {"center": v(-15.14, 400.05) * mm, "radius": 4.76 * mm});
            skCircle(sketch, "E35.0.5.6", {"center": v(-15.14, 381) * mm, "radius": 4.76 * mm});
            skArc(sketch, "E35.0.5.7", {"start": v(-10.38, 420.69) * mm, "mid": v(-15.14, 425.45) * mm, "end": v(-19.9, 420.69) * mm});
            skArc(sketch, "E35.0.5.8", {"start": v(-19.9, 417.51) * mm, "mid": v(-15.14, 412.75) * mm, "end": v(-10.38, 417.51) * mm});
            skPoint(sketch, "E35.0.5.9", {"position": v(-15.14, 438.15) * mm});
            skPoint(sketch, "E35.0.5.10", {"position": v(-15.14, 419.1) * mm});
            skLineSegment(sketch, "E35.0.5.11", {"start": v(-19.9, 439.74) * mm, "end": v(-19.9, 436.56) * mm});
            skLineSegment(sketch, "E35.0.5.12", {"start": v(-10.38, 439.74) * mm, "end": v(-10.38, 436.56) * mm});
            skLineSegment(sketch, "E35.0.5.13", {"start": v(-10.38, 420.69) * mm, "end": v(-10.38, 417.51) * mm});
            skLineSegment(sketch, "E35.0.5.14", {"start": v(-19.9, 420.69) * mm, "end": v(-19.9, 417.51) * mm});
            skPoint(sketch, "E35.0.6.0", {"position": v(-15.14, 514.35) * mm});
            skArc(sketch, "E35.0.6.1", {"start": v(-10.38, 515.94) * mm, "mid": v(-15.14, 520.7) * mm, "end": v(-19.9, 515.94) * mm});
            skPoint(sketch, "E35.0.6.2", {"position": v(-15.14, 495.3) * mm});
            skPoint(sketch, "E35.0.6.3", {"position": v(-15.14, 476.25) * mm});
            skArc(sketch, "E35.0.6.4", {"start": v(-19.9, 512.76) * mm, "mid": v(-15.14, 508) * mm, "end": v(-10.38, 512.76) * mm});
            skCircle(sketch, "E35.0.6.5", {"center": v(-15.14, 476.25) * mm, "radius": 4.76 * mm});
            skCircle(sketch, "E35.0.6.6", {"center": v(-15.14, 457.2) * mm, "radius": 4.76 * mm});
            skArc(sketch, "E35.0.6.7", {"start": v(-10.38, 496.89) * mm, "mid": v(-15.14, 501.65) * mm, "end": v(-19.9, 496.89) * mm});
            skArc(sketch, "E35.0.6.8", {"start": v(-19.9, 493.71) * mm, "mid": v(-15.14, 488.95) * mm, "end": v(-10.38, 493.71) * mm});
            skPoint(sketch, "E35.0.6.9", {"position": v(-15.14, 514.35) * mm});
            skPoint(sketch, "E35.0.6.10", {"position": v(-15.14, 495.3) * mm});
            skLineSegment(sketch, "E35.0.6.11", {"start": v(-19.9, 515.94) * mm, "end": v(-19.9, 512.76) * mm});
            skLineSegment(sketch, "E35.0.6.12", {"start": v(-10.38, 515.94) * mm, "end": v(-10.38, 512.76) * mm});
            skLineSegment(sketch, "E35.0.6.13", {"start": v(-10.38, 496.89) * mm, "end": v(-10.38, 493.71) * mm});
            skLineSegment(sketch, "E35.0.6.14", {"start": v(-19.9, 496.89) * mm, "end": v(-19.9, 493.71) * mm});
            skPoint(sketch, "E35.0.7.0", {"position": v(-15.14, 590.55) * mm});
            skArc(sketch, "E35.0.7.1", {"start": v(-10.38, 592.14) * mm, "mid": v(-15.14, 596.9) * mm, "end": v(-19.9, 592.14) * mm});
            skPoint(sketch, "E35.0.7.2", {"position": v(-15.14, 571.5) * mm});
            skPoint(sketch, "E35.0.7.3", {"position": v(-15.14, 552.45) * mm});
            skArc(sketch, "E35.0.7.4", {"start": v(-19.9, 588.96) * mm, "mid": v(-15.14, 584.2) * mm, "end": v(-10.38, 588.96) * mm});
            skCircle(sketch, "E35.0.7.5", {"center": v(-15.14, 552.45) * mm, "radius": 4.76 * mm});
            skCircle(sketch, "E35.0.7.6", {"center": v(-15.14, 533.4) * mm, "radius": 4.76 * mm});
            skArc(sketch, "E35.0.7.7", {"start": v(-10.38, 573.09) * mm, "mid": v(-15.14, 577.85) * mm, "end": v(-19.9, 573.09) * mm});
            skArc(sketch, "E35.0.7.8", {"start": v(-19.9, 569.91) * mm, "mid": v(-15.14, 565.15) * mm, "end": v(-10.38, 569.91) * mm});
            skPoint(sketch, "E35.0.7.9", {"position": v(-15.14, 590.55) * mm});
            skPoint(sketch, "E35.0.7.10", {"position": v(-15.14, 571.5) * mm});
            skLineSegment(sketch, "E35.0.7.11", {"start": v(-19.9, 592.14) * mm, "end": v(-19.9, 588.96) * mm});
            skLineSegment(sketch, "E35.0.7.12", {"start": v(-10.38, 592.14) * mm, "end": v(-10.38, 588.96) * mm});
            skLineSegment(sketch, "E35.0.7.13", {"start": v(-10.38, 573.09) * mm, "end": v(-10.38, 569.91) * mm});
            skLineSegment(sketch, "E35.0.7.14", {"start": v(-19.9, 573.09) * mm, "end": v(-19.9, 569.91) * mm});
            skPoint(sketch, "E35.0.8.0", {"position": v(-15.14, 666.75) * mm});
            skArc(sketch, "E35.0.8.1", {"start": v(-10.38, 668.34) * mm, "mid": v(-15.14, 673.1) * mm, "end": v(-19.9, 668.34) * mm});
            skPoint(sketch, "E35.0.8.2", {"position": v(-15.14, 647.7) * mm});
            skPoint(sketch, "E35.0.8.3", {"position": v(-15.14, 628.65) * mm});
            skArc(sketch, "E35.0.8.4", {"start": v(-19.9, 665.16) * mm, "mid": v(-15.14, 660.4) * mm, "end": v(-10.38, 665.16) * mm});
            skCircle(sketch, "E35.0.8.5", {"center": v(-15.14, 628.65) * mm, "radius": 4.76 * mm});
            skCircle(sketch, "E35.0.8.6", {"center": v(-15.14, 609.6) * mm, "radius": 4.76 * mm});
            skArc(sketch, "E35.0.8.7", {"start": v(-10.38, 649.29) * mm, "mid": v(-15.14, 654.05) * mm, "end": v(-19.9, 649.29) * mm});
            skArc(sketch, "E35.0.8.8", {"start": v(-19.9, 646.11) * mm, "mid": v(-15.14, 641.35) * mm, "end": v(-10.38, 646.11) * mm});
            skPoint(sketch, "E35.0.8.9", {"position": v(-15.14, 666.75) * mm});
            skPoint(sketch, "E35.0.8.10", {"position": v(-15.14, 647.7) * mm});
            skLineSegment(sketch, "E35.0.8.11", {"start": v(-19.9, 668.34) * mm, "end": v(-19.9, 665.16) * mm});
            skLineSegment(sketch, "E35.0.8.12", {"start": v(-10.38, 668.34) * mm, "end": v(-10.38, 665.16) * mm});
            skLineSegment(sketch, "E35.0.8.13", {"start": v(-10.38, 649.29) * mm, "end": v(-10.38, 646.11) * mm});
            skLineSegment(sketch, "E35.0.8.14", {"start": v(-19.9, 649.29) * mm, "end": v(-19.9, 646.11) * mm});
            skPoint(sketch, "E35.0.9.0", {"position": v(-15.14, 742.95) * mm});
            skArc(sketch, "E35.0.9.1", {"start": v(-10.38, 744.54) * mm, "mid": v(-15.14, 749.3) * mm, "end": v(-19.9, 744.54) * mm});
            skPoint(sketch, "E35.0.9.2", {"position": v(-15.14, 723.9) * mm});
            skPoint(sketch, "E35.0.9.3", {"position": v(-15.14, 704.85) * mm});
            skArc(sketch, "E35.0.9.4", {"start": v(-19.9, 741.36) * mm, "mid": v(-15.14, 736.6) * mm, "end": v(-10.38, 741.36) * mm});
            skCircle(sketch, "E35.0.9.5", {"center": v(-15.14, 704.85) * mm, "radius": 4.76 * mm});
            skCircle(sketch, "E35.0.9.6", {"center": v(-15.14, 685.8) * mm, "radius": 4.76 * mm});
            skArc(sketch, "E35.0.9.7", {"start": v(-10.38, 725.49) * mm, "mid": v(-15.14, 730.25) * mm, "end": v(-19.9, 725.49) * mm});
            skArc(sketch, "E35.0.9.8", {"start": v(-19.9, 722.31) * mm, "mid": v(-15.14, 717.55) * mm, "end": v(-10.38, 722.31) * mm});
            skPoint(sketch, "E35.0.9.9", {"position": v(-15.14, 742.95) * mm});
            skPoint(sketch, "E35.0.9.10", {"position": v(-15.14, 723.9) * mm});
            skLineSegment(sketch, "E35.0.9.11", {"start": v(-19.9, 744.54) * mm, "end": v(-19.9, 741.36) * mm});
            skLineSegment(sketch, "E35.0.9.12", {"start": v(-10.38, 744.54) * mm, "end": v(-10.38, 741.36) * mm});
            skLineSegment(sketch, "E35.0.9.13", {"start": v(-10.38, 725.49) * mm, "end": v(-10.38, 722.31) * mm});
            skLineSegment(sketch, "E35.0.9.14", {"start": v(-19.9, 725.49) * mm, "end": v(-19.9, 722.31) * mm});
            skPoint(sketch, "E35.0.10.0", {"position": v(-15.14, 819.15) * mm});
            skArc(sketch, "E35.0.10.1", {"start": v(-10.38, 820.74) * mm, "mid": v(-15.14, 825.5) * mm, "end": v(-19.9, 820.74) * mm});
            skPoint(sketch, "E35.0.10.2", {"position": v(-15.14, 800.1) * mm});
            skPoint(sketch, "E35.0.10.3", {"position": v(-15.14, 781.05) * mm});
            skArc(sketch, "E35.0.10.4", {"start": v(-19.9, 817.56) * mm, "mid": v(-15.14, 812.8) * mm, "end": v(-10.38, 817.56) * mm});
            skCircle(sketch, "E35.0.10.5", {"center": v(-15.14, 781.05) * mm, "radius": 4.76 * mm});
            skCircle(sketch, "E35.0.10.6", {"center": v(-15.14, 762) * mm, "radius": 4.76 * mm});
            skArc(sketch, "E35.0.10.7", {"start": v(-10.38, 801.69) * mm, "mid": v(-15.14, 806.45) * mm, "end": v(-19.9, 801.69) * mm});
            skArc(sketch, "E35.0.10.8", {"start": v(-19.9, 798.51) * mm, "mid": v(-15.14, 793.75) * mm, "end": v(-10.38, 798.51) * mm});
            skPoint(sketch, "E35.0.10.9", {"position": v(-15.14, 819.15) * mm});
            skPoint(sketch, "E35.0.10.10", {"position": v(-15.14, 800.1) * mm});
            skLineSegment(sketch, "E35.0.10.11", {"start": v(-19.9, 820.74) * mm, "end": v(-19.9, 817.56) * mm});
            skLineSegment(sketch, "E35.0.10.12", {"start": v(-10.38, 820.74) * mm, "end": v(-10.38, 817.56) * mm});
            skLineSegment(sketch, "E35.0.10.13", {"start": v(-10.38, 801.69) * mm, "end": v(-10.38, 798.51) * mm});
            skLineSegment(sketch, "E35.0.10.14", {"start": v(-19.9, 801.69) * mm, "end": v(-19.9, 798.51) * mm});
            skPoint(sketch, "E35.0.11.0", {"position": v(-15.14, 895.35) * mm});
            skArc(sketch, "E35.0.11.1", {"start": v(-10.38, 896.94) * mm, "mid": v(-15.14, 901.7) * mm, "end": v(-19.9, 896.94) * mm});
            skPoint(sketch, "E35.0.11.2", {"position": v(-15.14, 876.3) * mm});
            skPoint(sketch, "E35.0.11.3", {"position": v(-15.14, 857.25) * mm});
            skArc(sketch, "E35.0.11.4", {"start": v(-19.9, 893.76) * mm, "mid": v(-15.14, 889) * mm, "end": v(-10.38, 893.76) * mm});
            skCircle(sketch, "E35.0.11.5", {"center": v(-15.14, 857.25) * mm, "radius": 4.76 * mm});
            skCircle(sketch, "E35.0.11.6", {"center": v(-15.14, 838.2) * mm, "radius": 4.76 * mm});
            skArc(sketch, "E35.0.11.7", {"start": v(-10.38, 877.89) * mm, "mid": v(-15.14, 882.65) * mm, "end": v(-19.9, 877.89) * mm});
            skArc(sketch, "E35.0.11.8", {"start": v(-19.9, 874.71) * mm, "mid": v(-15.14, 869.95) * mm, "end": v(-10.38, 874.71) * mm});
            skPoint(sketch, "E35.0.11.9", {"position": v(-15.14, 895.35) * mm});
            skPoint(sketch, "E35.0.11.10", {"position": v(-15.14, 876.3) * mm});
            skLineSegment(sketch, "E35.0.11.11", {"start": v(-19.9, 896.94) * mm, "end": v(-19.9, 893.76) * mm});
            skLineSegment(sketch, "E35.0.11.12", {"start": v(-10.38, 896.94) * mm, "end": v(-10.38, 893.76) * mm});
            skLineSegment(sketch, "E35.0.11.13", {"start": v(-10.38, 877.89) * mm, "end": v(-10.38, 874.71) * mm});
            skLineSegment(sketch, "E35.0.11.14", {"start": v(-19.9, 877.89) * mm, "end": v(-19.9, 874.71) * mm});
            skPoint(sketch, "E35.0.12.0", {"position": v(-15.14, 971.55) * mm});
            skArc(sketch, "E35.0.12.1", {"start": v(-10.38, 973.14) * mm, "mid": v(-15.14, 977.9) * mm, "end": v(-19.9, 973.14) * mm});
            skPoint(sketch, "E35.0.12.2", {"position": v(-15.14, 952.5) * mm});
            skPoint(sketch, "E35.0.12.3", {"position": v(-15.14, 933.45) * mm});
            skArc(sketch, "E35.0.12.4", {"start": v(-19.9, 969.96) * mm, "mid": v(-15.14, 965.2) * mm, "end": v(-10.38, 969.96) * mm});
            skCircle(sketch, "E35.0.12.5", {"center": v(-15.14, 933.45) * mm, "radius": 4.76 * mm});
            skCircle(sketch, "E35.0.12.6", {"center": v(-15.14, 914.4) * mm, "radius": 4.76 * mm});
            skArc(sketch, "E35.0.12.7", {"start": v(-10.38, 954.09) * mm, "mid": v(-15.14, 958.85) * mm, "end": v(-19.9, 954.09) * mm});
            skArc(sketch, "E35.0.12.8", {"start": v(-19.9, 950.91) * mm, "mid": v(-15.14, 946.15) * mm, "end": v(-10.38, 950.91) * mm});
            skPoint(sketch, "E35.0.12.9", {"position": v(-15.14, 971.55) * mm});
            skPoint(sketch, "E35.0.12.10", {"position": v(-15.14, 952.5) * mm});
            skLineSegment(sketch, "E35.0.12.11", {"start": v(-19.9, 973.14) * mm, "end": v(-19.9, 969.96) * mm});
            skLineSegment(sketch, "E35.0.12.12", {"start": v(-10.38, 973.14) * mm, "end": v(-10.38, 969.96) * mm});
            skLineSegment(sketch, "E35.0.12.13", {"start": v(-10.38, 954.09) * mm, "end": v(-10.38, 950.91) * mm});
            skLineSegment(sketch, "E35.0.12.14", {"start": v(-19.9, 954.09) * mm, "end": v(-19.9, 950.91) * mm});
            skPoint(sketch, "E35.0.13.0", {"position": v(-15.14, 1047.75) * mm});
            skArc(sketch, "E35.0.13.1", {"start": v(-10.38, 1049.34) * mm, "mid": v(-15.14, 1054.1) * mm, "end": v(-19.9, 1049.34) * mm});
            skPoint(sketch, "E35.0.13.2", {"position": v(-15.14, 1028.7) * mm});
            skPoint(sketch, "E35.0.13.3", {"position": v(-15.14, 1009.65) * mm});
            skArc(sketch, "E35.0.13.4", {"start": v(-19.9, 1046.16) * mm, "mid": v(-15.14, 1041.4) * mm, "end": v(-10.38, 1046.16) * mm});
            skCircle(sketch, "E35.0.13.5", {"center": v(-15.14, 1009.65) * mm, "radius": 4.76 * mm});
            skCircle(sketch, "E35.0.13.6", {"center": v(-15.14, 990.6) * mm, "radius": 4.76 * mm});
            skArc(sketch, "E35.0.13.7", {"start": v(-10.38, 1030.29) * mm, "mid": v(-15.14, 1035.05) * mm, "end": v(-19.9, 1030.29) * mm});
            skArc(sketch, "E35.0.13.8", {"start": v(-19.9, 1027.11) * mm, "mid": v(-15.14, 1022.35) * mm, "end": v(-10.38, 1027.11) * mm});
            skPoint(sketch, "E35.0.13.9", {"position": v(-15.14, 1047.75) * mm});
            skPoint(sketch, "E35.0.13.10", {"position": v(-15.14, 1028.7) * mm});
            skLineSegment(sketch, "E35.0.13.11", {"start": v(-19.9, 1049.34) * mm, "end": v(-19.9, 1046.16) * mm});
            skLineSegment(sketch, "E35.0.13.12", {"start": v(-10.38, 1049.34) * mm, "end": v(-10.38, 1046.16) * mm});
            skLineSegment(sketch, "E35.0.13.13", {"start": v(-10.38, 1030.29) * mm, "end": v(-10.38, 1027.11) * mm});
            skLineSegment(sketch, "E35.0.13.14", {"start": v(-19.9, 1030.29) * mm, "end": v(-19.9, 1027.11) * mm});
            skPoint(sketch, "E35.0.14.0", {"position": v(-15.14, 1123.95) * mm});
            skArc(sketch, "E35.0.14.1", {"start": v(-10.38, 1125.54) * mm, "mid": v(-15.14, 1130.3) * mm, "end": v(-19.9, 1125.54) * mm});
            skPoint(sketch, "E35.0.14.2", {"position": v(-15.14, 1104.9) * mm});
            skPoint(sketch, "E35.0.14.3", {"position": v(-15.14, 1085.85) * mm});
            skArc(sketch, "E35.0.14.4", {"start": v(-19.9, 1122.36) * mm, "mid": v(-15.14, 1117.6) * mm, "end": v(-10.38, 1122.36) * mm});
            skCircle(sketch, "E35.0.14.5", {"center": v(-15.14, 1085.85) * mm, "radius": 4.76 * mm});
            skCircle(sketch, "E35.0.14.6", {"center": v(-15.14, 1066.8) * mm, "radius": 4.76 * mm});
            skArc(sketch, "E35.0.14.7", {"start": v(-10.38, 1106.49) * mm, "mid": v(-15.14, 1111.25) * mm, "end": v(-19.9, 1106.49) * mm});
            skArc(sketch, "E35.0.14.8", {"start": v(-19.9, 1103.31) * mm, "mid": v(-15.14, 1098.55) * mm, "end": v(-10.38, 1103.31) * mm});
            skPoint(sketch, "E35.0.14.9", {"position": v(-15.14, 1123.95) * mm});
            skPoint(sketch, "E35.0.14.10", {"position": v(-15.14, 1104.9) * mm});
            skLineSegment(sketch, "E35.0.14.11", {"start": v(-19.9, 1125.54) * mm, "end": v(-19.9, 1122.36) * mm});
            skLineSegment(sketch, "E35.0.14.12", {"start": v(-10.38, 1125.54) * mm, "end": v(-10.38, 1122.36) * mm});
            skLineSegment(sketch, "E35.0.14.13", {"start": v(-10.38, 1106.49) * mm, "end": v(-10.38, 1103.31) * mm});
            skLineSegment(sketch, "E35.0.14.14", {"start": v(-19.9, 1106.49) * mm, "end": v(-19.9, 1103.31) * mm});
            skPoint(sketch, "E35.0.15.0", {"position": v(-15.14, 1200.15) * mm});
            skArc(sketch, "E35.0.15.1", {"start": v(-10.38, 1201.74) * mm, "mid": v(-15.14, 1206.5) * mm, "end": v(-19.9, 1201.74) * mm});
            skPoint(sketch, "E35.0.15.2", {"position": v(-15.14, 1181.1) * mm});
            skPoint(sketch, "E35.0.15.3", {"position": v(-15.14, 1162.05) * mm});
            skArc(sketch, "E35.0.15.4", {"start": v(-19.9, 1198.56) * mm, "mid": v(-15.14, 1193.8) * mm, "end": v(-10.38, 1198.56) * mm});
            skCircle(sketch, "E35.0.15.5", {"center": v(-15.14, 1162.05) * mm, "radius": 4.76 * mm});
            skCircle(sketch, "E35.0.15.6", {"center": v(-15.14, 1143) * mm, "radius": 4.76 * mm});
            skArc(sketch, "E35.0.15.7", {"start": v(-10.38, 1182.69) * mm, "mid": v(-15.14, 1187.45) * mm, "end": v(-19.9, 1182.69) * mm});
            skArc(sketch, "E35.0.15.8", {"start": v(-19.9, 1179.51) * mm, "mid": v(-15.14, 1174.75) * mm, "end": v(-10.38, 1179.51) * mm});
            skPoint(sketch, "E35.0.15.9", {"position": v(-15.14, 1200.15) * mm});
            skPoint(sketch, "E35.0.15.10", {"position": v(-15.14, 1181.1) * mm});
            skLineSegment(sketch, "E35.0.15.11", {"start": v(-19.9, 1201.74) * mm, "end": v(-19.9, 1198.56) * mm});
            skLineSegment(sketch, "E35.0.15.12", {"start": v(-10.38, 1201.74) * mm, "end": v(-10.38, 1198.56) * mm});
            skLineSegment(sketch, "E35.0.15.13", {"start": v(-10.38, 1182.69) * mm, "end": v(-10.38, 1179.51) * mm});
            skLineSegment(sketch, "E35.0.15.14", {"start": v(-19.9, 1182.69) * mm, "end": v(-19.9, 1179.51) * mm});
            skPoint(sketch, "E35.0.16.0", {"position": v(-15.14, 1276.35) * mm});
            skArc(sketch, "E35.0.16.1", {"start": v(-10.38, 1277.94) * mm, "mid": v(-15.14, 1282.7) * mm, "end": v(-19.9, 1277.94) * mm});
            skPoint(sketch, "E35.0.16.2", {"position": v(-15.14, 1257.3) * mm});
            skPoint(sketch, "E35.0.16.3", {"position": v(-15.14, 1238.25) * mm});
            skArc(sketch, "E35.0.16.4", {"start": v(-19.9, 1274.76) * mm, "mid": v(-15.14, 1270) * mm, "end": v(-10.38, 1274.76) * mm});
            skCircle(sketch, "E35.0.16.5", {"center": v(-15.14, 1238.25) * mm, "radius": 4.76 * mm});
            skCircle(sketch, "E35.0.16.6", {"center": v(-15.14, 1219.2) * mm, "radius": 4.76 * mm});
            skArc(sketch, "E35.0.16.7", {"start": v(-10.38, 1258.89) * mm, "mid": v(-15.14, 1263.65) * mm, "end": v(-19.9, 1258.89) * mm});
            skArc(sketch, "E35.0.16.8", {"start": v(-19.9, 1255.71) * mm, "mid": v(-15.14, 1250.95) * mm, "end": v(-10.38, 1255.71) * mm});
            skPoint(sketch, "E35.0.16.9", {"position": v(-15.14, 1276.35) * mm});
            skPoint(sketch, "E35.0.16.10", {"position": v(-15.14, 1257.3) * mm});
            skLineSegment(sketch, "E35.0.16.11", {"start": v(-19.9, 1277.94) * mm, "end": v(-19.9, 1274.76) * mm});
            skLineSegment(sketch, "E35.0.16.12", {"start": v(-10.38, 1277.94) * mm, "end": v(-10.38, 1274.76) * mm});
            skLineSegment(sketch, "E35.0.16.13", {"start": v(-10.38, 1258.89) * mm, "end": v(-10.38, 1255.71) * mm});
            skLineSegment(sketch, "E35.0.16.14", {"start": v(-19.9, 1258.89) * mm, "end": v(-19.9, 1255.71) * mm});
            skPoint(sketch, "E35.0.17.0", {"position": v(-15.14, 1352.55) * mm});
            skArc(sketch, "E35.0.17.1", {"start": v(-10.38, 1354.14) * mm, "mid": v(-15.14, 1358.9) * mm, "end": v(-19.9, 1354.14) * mm});
            skPoint(sketch, "E35.0.17.2", {"position": v(-15.14, 1333.5) * mm});
            skPoint(sketch, "E35.0.17.3", {"position": v(-15.14, 1314.45) * mm});
            skArc(sketch, "E35.0.17.4", {"start": v(-19.9, 1350.96) * mm, "mid": v(-15.14, 1346.2) * mm, "end": v(-10.38, 1350.96) * mm});
            skCircle(sketch, "E35.0.17.5", {"center": v(-15.14, 1314.45) * mm, "radius": 4.76 * mm});
            skCircle(sketch, "E35.0.17.6", {"center": v(-15.14, 1295.4) * mm, "radius": 4.76 * mm});
            skArc(sketch, "E35.0.17.7", {"start": v(-10.38, 1335.09) * mm, "mid": v(-15.14, 1339.85) * mm, "end": v(-19.9, 1335.09) * mm});
            skArc(sketch, "E35.0.17.8", {"start": v(-19.9, 1331.91) * mm, "mid": v(-15.14, 1327.15) * mm, "end": v(-10.38, 1331.91) * mm});
            skPoint(sketch, "E35.0.17.9", {"position": v(-15.14, 1352.55) * mm});
            skPoint(sketch, "E35.0.17.10", {"position": v(-15.14, 1333.5) * mm});
            skLineSegment(sketch, "E35.0.17.11", {"start": v(-19.9, 1354.14) * mm, "end": v(-19.9, 1350.96) * mm});
            skLineSegment(sketch, "E35.0.17.12", {"start": v(-10.38, 1354.14) * mm, "end": v(-10.38, 1350.96) * mm});
            skLineSegment(sketch, "E35.0.17.13", {"start": v(-10.38, 1335.09) * mm, "end": v(-10.38, 1331.91) * mm});
            skLineSegment(sketch, "E35.0.17.14", {"start": v(-19.9, 1335.09) * mm, "end": v(-19.9, 1331.91) * mm});
            skPoint(sketch, "E35.0.18.0", {"position": v(-15.14, 1428.75) * mm});
            skArc(sketch, "E35.0.18.1", {"start": v(-10.38, 1430.34) * mm, "mid": v(-15.14, 1435.1) * mm, "end": v(-19.9, 1430.34) * mm});
            skPoint(sketch, "E35.0.18.2", {"position": v(-15.14, 1409.7) * mm});
            skPoint(sketch, "E35.0.18.3", {"position": v(-15.14, 1390.65) * mm});
            skArc(sketch, "E35.0.18.4", {"start": v(-19.9, 1427.16) * mm, "mid": v(-15.14, 1422.4) * mm, "end": v(-10.38, 1427.16) * mm});
            skCircle(sketch, "E35.0.18.5", {"center": v(-15.14, 1390.65) * mm, "radius": 4.76 * mm});
            skCircle(sketch, "E35.0.18.6", {"center": v(-15.14, 1371.6) * mm, "radius": 4.76 * mm});
            skArc(sketch, "E35.0.18.7", {"start": v(-10.38, 1411.29) * mm, "mid": v(-15.14, 1416.05) * mm, "end": v(-19.9, 1411.29) * mm});
            skArc(sketch, "E35.0.18.8", {"start": v(-19.9, 1408.11) * mm, "mid": v(-15.14, 1403.35) * mm, "end": v(-10.38, 1408.11) * mm});
            skPoint(sketch, "E35.0.18.9", {"position": v(-15.14, 1428.75) * mm});
            skPoint(sketch, "E35.0.18.10", {"position": v(-15.14, 1409.7) * mm});
            skLineSegment(sketch, "E35.0.18.11", {"start": v(-19.9, 1430.34) * mm, "end": v(-19.9, 1427.16) * mm});
            skLineSegment(sketch, "E35.0.18.12", {"start": v(-10.38, 1430.34) * mm, "end": v(-10.38, 1427.16) * mm});
            skLineSegment(sketch, "E35.0.18.13", {"start": v(-10.38, 1411.29) * mm, "end": v(-10.38, 1408.11) * mm});
            skLineSegment(sketch, "E35.0.18.14", {"start": v(-19.9, 1411.29) * mm, "end": v(-19.9, 1408.11) * mm});
            skPoint(sketch, "E35.0.19.0", {"position": v(-15.14, 1504.95) * mm});
            skArc(sketch, "E35.0.19.1", {"start": v(-10.38, 1506.54) * mm, "mid": v(-15.14, 1511.3) * mm, "end": v(-19.9, 1506.54) * mm});
            skPoint(sketch, "E35.0.19.2", {"position": v(-15.14, 1485.9) * mm});
            skPoint(sketch, "E35.0.19.3", {"position": v(-15.14, 1466.85) * mm});
            skArc(sketch, "E35.0.19.4", {"start": v(-19.9, 1503.36) * mm, "mid": v(-15.14, 1498.6) * mm, "end": v(-10.38, 1503.36) * mm});
            skCircle(sketch, "E35.0.19.5", {"center": v(-15.14, 1466.85) * mm, "radius": 4.76 * mm});
            skCircle(sketch, "E35.0.19.6", {"center": v(-15.14, 1447.8) * mm, "radius": 4.76 * mm});
            skArc(sketch, "E35.0.19.7", {"start": v(-10.38, 1487.49) * mm, "mid": v(-15.14, 1492.25) * mm, "end": v(-19.9, 1487.49) * mm});
            skArc(sketch, "E35.0.19.8", {"start": v(-19.9, 1484.31) * mm, "mid": v(-15.14, 1479.55) * mm, "end": v(-10.38, 1484.31) * mm});
            skPoint(sketch, "E35.0.19.9", {"position": v(-15.14, 1504.95) * mm});
            skPoint(sketch, "E35.0.19.10", {"position": v(-15.14, 1485.9) * mm});
            skLineSegment(sketch, "E35.0.19.11", {"start": v(-19.9, 1506.54) * mm, "end": v(-19.9, 1503.36) * mm});
            skLineSegment(sketch, "E35.0.19.12", {"start": v(-10.38, 1506.54) * mm, "end": v(-10.38, 1503.36) * mm});
            skLineSegment(sketch, "E35.0.19.13", {"start": v(-10.38, 1487.49) * mm, "end": v(-10.38, 1484.31) * mm});
            skLineSegment(sketch, "E35.0.19.14", {"start": v(-19.9, 1487.49) * mm, "end": v(-19.9, 1484.31) * mm});
            skPoint(sketch, "E35.0.20.0", {"position": v(-15.14, 1581.15) * mm});
            skArc(sketch, "E35.0.20.1", {"start": v(-10.38, 1582.74) * mm, "mid": v(-15.14, 1587.5) * mm, "end": v(-19.9, 1582.74) * mm});
            skPoint(sketch, "E35.0.20.2", {"position": v(-15.14, 1562.1) * mm});
            skPoint(sketch, "E35.0.20.3", {"position": v(-15.14, 1543.05) * mm});
            skArc(sketch, "E35.0.20.4", {"start": v(-19.9, 1579.56) * mm, "mid": v(-15.14, 1574.8) * mm, "end": v(-10.38, 1579.56) * mm});
            skCircle(sketch, "E35.0.20.5", {"center": v(-15.14, 1543.05) * mm, "radius": 4.76 * mm});
            skCircle(sketch, "E35.0.20.6", {"center": v(-15.14, 1524) * mm, "radius": 4.76 * mm});
            skArc(sketch, "E35.0.20.7", {"start": v(-10.38, 1563.69) * mm, "mid": v(-15.14, 1568.45) * mm, "end": v(-19.9, 1563.69) * mm});
            skArc(sketch, "E35.0.20.8", {"start": v(-19.9, 1560.51) * mm, "mid": v(-15.14, 1555.75) * mm, "end": v(-10.38, 1560.51) * mm});
            skPoint(sketch, "E35.0.20.9", {"position": v(-15.14, 1581.15) * mm});
            skPoint(sketch, "E35.0.20.10", {"position": v(-15.14, 1562.1) * mm});
            skLineSegment(sketch, "E35.0.20.11", {"start": v(-19.9, 1582.74) * mm, "end": v(-19.9, 1579.56) * mm});
            skLineSegment(sketch, "E35.0.20.12", {"start": v(-10.38, 1582.74) * mm, "end": v(-10.38, 1579.56) * mm});
            skLineSegment(sketch, "E35.0.20.13", {"start": v(-10.38, 1563.69) * mm, "end": v(-10.38, 1560.51) * mm});
            skLineSegment(sketch, "E35.0.20.14", {"start": v(-19.9, 1563.69) * mm, "end": v(-19.9, 1560.51) * mm});
            skPoint(sketch, "E35.0.21.0", {"position": v(-15.14, 1657.35) * mm});
            skArc(sketch, "E35.0.21.1", {"start": v(-10.38, 1658.94) * mm, "mid": v(-15.14, 1663.7) * mm, "end": v(-19.9, 1658.94) * mm});
            skPoint(sketch, "E35.0.21.2", {"position": v(-15.14, 1638.3) * mm});
            skPoint(sketch, "E35.0.21.3", {"position": v(-15.14, 1619.25) * mm});
            skArc(sketch, "E35.0.21.4", {"start": v(-19.9, 1655.76) * mm, "mid": v(-15.14, 1651) * mm, "end": v(-10.38, 1655.76) * mm});
            skCircle(sketch, "E35.0.21.5", {"center": v(-15.14, 1619.25) * mm, "radius": 4.76 * mm});
            skCircle(sketch, "E35.0.21.6", {"center": v(-15.14, 1600.2) * mm, "radius": 4.76 * mm});
            skArc(sketch, "E35.0.21.7", {"start": v(-10.38, 1639.89) * mm, "mid": v(-15.14, 1644.65) * mm, "end": v(-19.9, 1639.89) * mm});
            skArc(sketch, "E35.0.21.8", {"start": v(-19.9, 1636.71) * mm, "mid": v(-15.14, 1631.95) * mm, "end": v(-10.38, 1636.71) * mm});
            skPoint(sketch, "E35.0.21.9", {"position": v(-15.14, 1657.35) * mm});
            skPoint(sketch, "E35.0.21.10", {"position": v(-15.14, 1638.3) * mm});
            skLineSegment(sketch, "E35.0.21.11", {"start": v(-19.9, 1658.94) * mm, "end": v(-19.9, 1655.76) * mm});
            skLineSegment(sketch, "E35.0.21.12", {"start": v(-10.38, 1658.94) * mm, "end": v(-10.38, 1655.76) * mm});
            skLineSegment(sketch, "E35.0.21.13", {"start": v(-10.38, 1639.89) * mm, "end": v(-10.38, 1636.71) * mm});
            skLineSegment(sketch, "E35.0.21.14", {"start": v(-19.9, 1639.89) * mm, "end": v(-19.9, 1636.71) * mm});
            skPoint(sketch, "E35.0.22.0", {"position": v(-15.14, 1733.55) * mm});
            skArc(sketch, "E35.0.22.1", {"start": v(-10.38, 1735.14) * mm, "mid": v(-15.14, 1739.9) * mm, "end": v(-19.9, 1735.14) * mm});
            skPoint(sketch, "E35.0.22.2", {"position": v(-15.14, 1714.5) * mm});
            skPoint(sketch, "E35.0.22.3", {"position": v(-15.14, 1695.45) * mm});
            skArc(sketch, "E35.0.22.4", {"start": v(-19.9, 1731.96) * mm, "mid": v(-15.14, 1727.2) * mm, "end": v(-10.38, 1731.96) * mm});
            skCircle(sketch, "E35.0.22.5", {"center": v(-15.14, 1695.45) * mm, "radius": 4.76 * mm});
            skCircle(sketch, "E35.0.22.6", {"center": v(-15.14, 1676.4) * mm, "radius": 4.76 * mm});
            skArc(sketch, "E35.0.22.7", {"start": v(-10.38, 1716.09) * mm, "mid": v(-15.14, 1720.85) * mm, "end": v(-19.9, 1716.09) * mm});
            skArc(sketch, "E35.0.22.8", {"start": v(-19.9, 1712.91) * mm, "mid": v(-15.14, 1708.15) * mm, "end": v(-10.38, 1712.91) * mm});
            skPoint(sketch, "E35.0.22.9", {"position": v(-15.14, 1733.55) * mm});
            skPoint(sketch, "E35.0.22.10", {"position": v(-15.14, 1714.5) * mm});
            skLineSegment(sketch, "E35.0.22.11", {"start": v(-19.9, 1735.14) * mm, "end": v(-19.9, 1731.96) * mm});
            skLineSegment(sketch, "E35.0.22.12", {"start": v(-10.38, 1735.14) * mm, "end": v(-10.38, 1731.96) * mm});
            skLineSegment(sketch, "E35.0.22.13", {"start": v(-10.38, 1716.09) * mm, "end": v(-10.38, 1712.91) * mm});
            skLineSegment(sketch, "E35.0.22.14", {"start": v(-19.9, 1716.09) * mm, "end": v(-19.9, 1712.91) * mm});
            skPoint(sketch, "E35.0.23.0", {"position": v(-15.14, 1809.75) * mm});
            skArc(sketch, "E35.0.23.1", {"start": v(-10.38, 1811.34) * mm, "mid": v(-15.14, 1816.1) * mm, "end": v(-19.9, 1811.34) * mm});
            skPoint(sketch, "E35.0.23.2", {"position": v(-15.14, 1790.7) * mm});
            skPoint(sketch, "E35.0.23.3", {"position": v(-15.14, 1771.65) * mm});
            skArc(sketch, "E35.0.23.4", {"start": v(-19.9, 1808.16) * mm, "mid": v(-15.14, 1803.4) * mm, "end": v(-10.38, 1808.16) * mm});
            skCircle(sketch, "E35.0.23.5", {"center": v(-15.14, 1771.65) * mm, "radius": 4.76 * mm});
            skCircle(sketch, "E35.0.23.6", {"center": v(-15.14, 1752.6) * mm, "radius": 4.76 * mm});
            skArc(sketch, "E35.0.23.7", {"start": v(-10.38, 1792.29) * mm, "mid": v(-15.14, 1797.05) * mm, "end": v(-19.9, 1792.29) * mm});
            skArc(sketch, "E35.0.23.8", {"start": v(-19.9, 1789.11) * mm, "mid": v(-15.14, 1784.35) * mm, "end": v(-10.38, 1789.11) * mm});
            skPoint(sketch, "E35.0.23.9", {"position": v(-15.14, 1809.75) * mm});
            skPoint(sketch, "E35.0.23.10", {"position": v(-15.14, 1790.7) * mm});
            skLineSegment(sketch, "E35.0.23.11", {"start": v(-19.9, 1811.34) * mm, "end": v(-19.9, 1808.16) * mm});
            skLineSegment(sketch, "E35.0.23.12", {"start": v(-10.38, 1811.34) * mm, "end": v(-10.38, 1808.16) * mm});
            skLineSegment(sketch, "E35.0.23.13", {"start": v(-10.38, 1792.29) * mm, "end": v(-10.38, 1789.11) * mm});
            skLineSegment(sketch, "E35.0.23.14", {"start": v(-19.9, 1792.29) * mm, "end": v(-19.9, 1789.11) * mm});
            skLineSegment(sketch, "E35.direction1", {"start": v(-15.14, 0) * mm, "end": v(10.99, 0) * mm, "construction": true});
            skLineSegment(sketch, "E35.direction2", {"start": v(-15.14, 0) * mm, "end": v(-15.14, 76.2) * mm, "construction": true});
            skSolve(sketch);
        }
        {
            var Q0;
            Q0=qSketchRegion(id+"F3",true);
            extrude(context, id + "F5", {"entities" : qUnion([Q0]), "operationType" : NewBodyOperationType.REMOVE, "endBound" : BoundingType.THROUGH_ALL, "oppositeDirection" : true, "depth" : 25.4 * mm, "offsetDistance" : 25.4 * mm});
        }
        {
            var Q0;
            Q0=qSketchRegion(id+"F4",true);
            extrude(context, id + "F6", {"entities" : qUnion([Q0]), "operationType" : NewBodyOperationType.REMOVE, "endBound" : BoundingType.THROUGH_ALL, "oppositeDirection" : true, "depth" : 25.4 * mm, "offsetDistance" : 25.4 * mm});
        }
        {
            var Q0;
            Q0=makeQuery(id+"F2.opExtrude","SWEPT_FACE",FACE,{"disambiguationData":[OSD([sQuery(id+"F1.wireOp",EDGE,"E1")])]});
            var sketch = newSketch(context, id + "F7", { "sketchPlane" : qUnion([Q0])});
            skLineSegment(sketch, "E36", {"start": v(1.37, 533.4) * mm, "end": v(-28.75, 533.4) * mm});
            skLineSegment(sketch, "E37", {"start": v(-28.75, 533.4) * mm, "end": v(-28.75, 503.28) * mm});
            skLineSegment(sketch, "E38", {"start": v(-28.75, 503.28) * mm, "end": v(1.37, 533.4) * mm});
            skLineSegment(sketch, "E39", {"start": v(-28.75, 0) * mm, "end": v(1.37, 0) * mm});
            skLineSegment(sketch, "E40", {"start": v(1.37, 0) * mm, "end": v(-28.75, 30.12) * mm});
            skLineSegment(sketch, "E41", {"start": v(-28.75, 30.12) * mm, "end": v(-28.75, 0) * mm});
            skSolve(sketch);
        }
        {
            var Q0;
            Q0=qSketchRegion(id+"F7",true);
            extrude(context, id + "F8", {"entities" : qUnion([Q0]), "operationType" : NewBodyOperationType.REMOVE, "endBound" : BoundingType.THROUGH_ALL, "oppositeDirection" : true, "depth" : 25.4 * mm, "offsetDistance" : 25.4 * mm});
        }
    });
